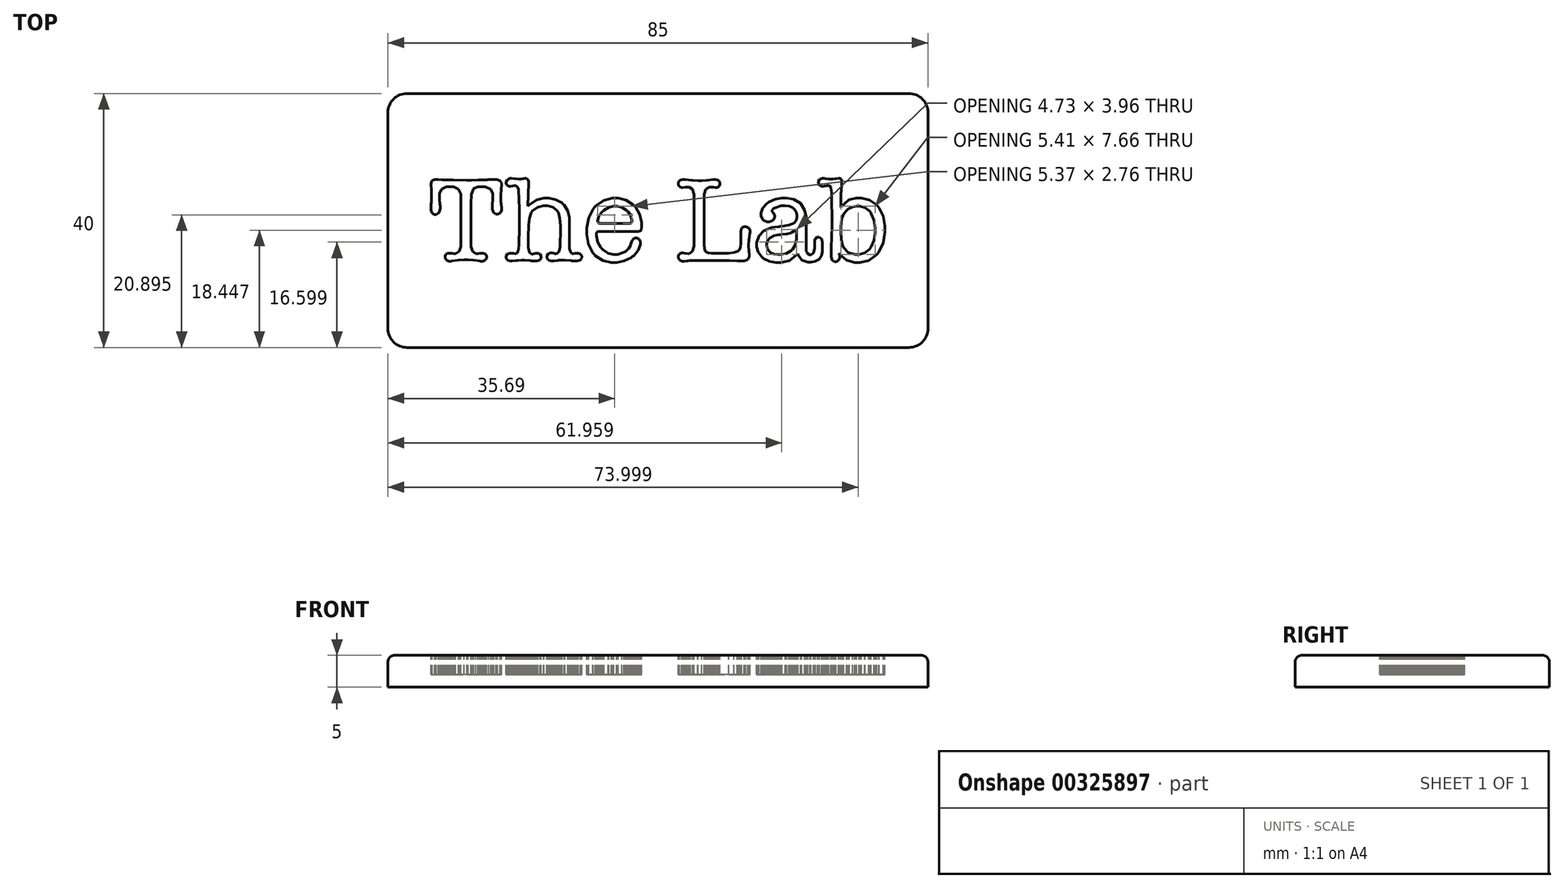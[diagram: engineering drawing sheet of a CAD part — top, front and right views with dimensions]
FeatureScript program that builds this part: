
annotation { "Feature Type Name" : "Feature", "Feature Type Description" : "" }
export const myFeature = defineFeature(function(context is Context, id is Id, definition is map)
    precondition{}
    {
        {
            var Q0;
            Q0=qCreatedBy(makeId("Top.planeOp"),FACE);
            var sketch = newSketch(context, id + "F0", { "sketchPlane" : qUnion([Q0])});
            skLineSegment(sketch, "E0", {"start": v(-29.44, -3.8) * mm, "end": v(-29.44, -4.07) * mm});
            skLineSegment(sketch, "E1", {"start": v(-29.44, -4.07) * mm, "end": v(-29.2, -4.87) * mm});
            skLineSegment(sketch, "E2", {"start": v(-29.2, -4.87) * mm, "end": v(-28.65, -5.23) * mm});
            skLineSegment(sketch, "E3", {"start": v(-28.65, -5.23) * mm, "end": v(-28.47, -5.23) * mm});
            skLineSegment(sketch, "E4", {"start": v(-28.47, -5.23) * mm, "end": v(-28.36, -5.23) * mm});
            skLineSegment(sketch, "E5", {"start": v(-28.36, -5.23) * mm, "end": v(-28.06, -5.19) * mm});
            skLineSegment(sketch, "E6", {"start": v(-28.06, -5.19) * mm, "end": v(-28.01, -5.18) * mm});
            skLineSegment(sketch, "E7", {"start": v(-28.01, -5.18) * mm, "end": v(-27.96, -5.17) * mm});
            skLineSegment(sketch, "E8", {"start": v(-27.96, -5.17) * mm, "end": v(-27.66, -5.13) * mm});
            skLineSegment(sketch, "E9", {"start": v(-27.66, -5.13) * mm, "end": v(-27.56, -5.13) * mm});
            skLineSegment(sketch, "E10", {"start": v(-27.56, -5.13) * mm, "end": v(-27.45, -5.13) * mm});
            skLineSegment(sketch, "E11", {"start": v(-27.45, -5.13) * mm, "end": v(-27.16, -5.28) * mm});
            skLineSegment(sketch, "E12", {"start": v(-27.16, -5.28) * mm, "end": v(-27.13, -5.31) * mm});
            skLineSegment(sketch, "E13", {"start": v(-27.13, -5.31) * mm, "end": v(-27.1, -5.34) * mm});
            skLineSegment(sketch, "E14", {"start": v(-27.1, -5.34) * mm, "end": v(-26.95, -5.64) * mm});
            skLineSegment(sketch, "E15", {"start": v(-26.95, -5.64) * mm, "end": v(-26.95, -5.74) * mm});
            skLineSegment(sketch, "E16", {"start": v(-26.95, -5.74) * mm, "end": v(-26.95, -5.87) * mm});
            skLineSegment(sketch, "E17", {"start": v(-26.95, -5.87) * mm, "end": v(-27.16, -6.24) * mm});
            skLineSegment(sketch, "E18", {"start": v(-27.16, -6.24) * mm, "end": v(-27.64, -6.4) * mm});
            skLineSegment(sketch, "E19", {"start": v(-27.64, -6.4) * mm, "end": v(-27.8, -6.4) * mm});
            skLineSegment(sketch, "E20", {"start": v(-27.8, -6.4) * mm, "end": v(-27.92, -6.4) * mm});
            skLineSegment(sketch, "E21", {"start": v(-27.92, -6.4) * mm, "end": v(-27.93, -6.4) * mm});
            skLineSegment(sketch, "E22", {"start": v(-27.93, -6.4) * mm, "end": v(-28.02, -6.4) * mm});
            skLineSegment(sketch, "E23", {"start": v(-28.02, -6.4) * mm, "end": v(-28.05, -6.4) * mm});
            skLineSegment(sketch, "E24", {"start": v(-28.05, -6.4) * mm, "end": v(-28.98, -6.26) * mm});
            skLineSegment(sketch, "E25", {"start": v(-28.98, -6.26) * mm, "end": v(-29.07, -6.24) * mm});
            skLineSegment(sketch, "E26", {"start": v(-29.07, -6.24) * mm, "end": v(-29.9, -6.18) * mm});
            skLineSegment(sketch, "E27", {"start": v(-29.9, -6.18) * mm, "end": v(-30.18, -6.18) * mm});
            skLineSegment(sketch, "E28", {"start": v(-30.18, -6.18) * mm, "end": v(-30.5, -6.18) * mm});
            skLineSegment(sketch, "E29", {"start": v(-30.5, -6.18) * mm, "end": v(-31.37, -6.24) * mm});
            skLineSegment(sketch, "E30", {"start": v(-31.37, -6.24) * mm, "end": v(-31.46, -6.26) * mm});
            skLineSegment(sketch, "E31", {"start": v(-31.46, -6.26) * mm, "end": v(-32.41, -6.4) * mm});
            skLineSegment(sketch, "E32", {"start": v(-32.41, -6.4) * mm, "end": v(-32.45, -6.4) * mm});
            skLineSegment(sketch, "E33", {"start": v(-32.45, -6.4) * mm, "end": v(-32.53, -6.4) * mm});
            skLineSegment(sketch, "E34", {"start": v(-32.53, -6.4) * mm, "end": v(-32.55, -6.4) * mm});
            skLineSegment(sketch, "E35", {"start": v(-32.55, -6.4) * mm, "end": v(-32.68, -6.4) * mm});
            skLineSegment(sketch, "E36", {"start": v(-32.68, -6.4) * mm, "end": v(-32.84, -6.4) * mm});
            skLineSegment(sketch, "E37", {"start": v(-32.84, -6.4) * mm, "end": v(-33.3, -6.24) * mm});
            skLineSegment(sketch, "E38", {"start": v(-33.3, -6.24) * mm, "end": v(-33.52, -5.87) * mm});
            skLineSegment(sketch, "E39", {"start": v(-33.52, -5.87) * mm, "end": v(-33.52, -5.74) * mm});
            skLineSegment(sketch, "E40", {"start": v(-33.52, -5.74) * mm, "end": v(-33.52, -5.63) * mm});
            skLineSegment(sketch, "E41", {"start": v(-33.52, -5.63) * mm, "end": v(-33.37, -5.29) * mm});
            skLineSegment(sketch, "E42", {"start": v(-33.37, -5.29) * mm, "end": v(-33.02, -5.13) * mm});
            skLineSegment(sketch, "E43", {"start": v(-33.02, -5.13) * mm, "end": v(-32.9, -5.13) * mm});
            skLineSegment(sketch, "E44", {"start": v(-32.9, -5.13) * mm, "end": v(-32.8, -5.13) * mm});
            skLineSegment(sketch, "E45", {"start": v(-32.8, -5.13) * mm, "end": v(-32.5, -5.17) * mm});
            skLineSegment(sketch, "E46", {"start": v(-32.5, -5.17) * mm, "end": v(-32.45, -5.18) * mm});
            skLineSegment(sketch, "E47", {"start": v(-32.45, -5.18) * mm, "end": v(-32.4, -5.19) * mm});
            skLineSegment(sketch, "E48", {"start": v(-32.4, -5.19) * mm, "end": v(-32.1, -5.23) * mm});
            skLineSegment(sketch, "E49", {"start": v(-32.1, -5.23) * mm, "end": v(-32, -5.23) * mm});
            skLineSegment(sketch, "E50", {"start": v(-32, -5.23) * mm, "end": v(-31.82, -5.23) * mm});
            skLineSegment(sketch, "E51", {"start": v(-31.82, -5.23) * mm, "end": v(-31.28, -4.87) * mm});
            skLineSegment(sketch, "E52", {"start": v(-31.28, -4.87) * mm, "end": v(-31.04, -4.07) * mm});
            skLineSegment(sketch, "E53", {"start": v(-31.04, -4.07) * mm, "end": v(-31.04, -3.8) * mm});
            skLineSegment(sketch, "E54", {"start": v(-31.04, -3.8) * mm, "end": v(-31.04, -2.47) * mm});
            skLineSegment(sketch, "E55", {"start": v(-31.04, -2.47) * mm, "end": v(-31.02, -0.8) * mm});
            skLineSegment(sketch, "E56", {"start": v(-31.02, -0.8) * mm, "end": v(-31.02, 0.83) * mm});
            skLineSegment(sketch, "E57", {"start": v(-31.02, 0.83) * mm, "end": v(-31.04, 3.93) * mm});
            skLineSegment(sketch, "E58", {"start": v(-31.04, 3.93) * mm, "end": v(-31.04, 4.19) * mm});
            skLineSegment(sketch, "E59", {"start": v(-31.04, 4.19) * mm, "end": v(-31.39, 4.95) * mm});
            skLineSegment(sketch, "E60", {"start": v(-31.39, 4.95) * mm, "end": v(-32.17, 5.29) * mm});
            skLineSegment(sketch, "E61", {"start": v(-32.17, 5.29) * mm, "end": v(-32.43, 5.29) * mm});
            skLineSegment(sketch, "E62", {"start": v(-32.43, 5.29) * mm, "end": v(-33.02, 5.29) * mm});
            skLineSegment(sketch, "E63", {"start": v(-33.02, 5.29) * mm, "end": v(-33.28, 5.29) * mm});
            skLineSegment(sketch, "E64", {"start": v(-33.28, 5.29) * mm, "end": v(-34.05, 4.95) * mm});
            skLineSegment(sketch, "E65", {"start": v(-34.05, 4.95) * mm, "end": v(-34.4, 4.2) * mm});
            skLineSegment(sketch, "E66", {"start": v(-34.4, 4.2) * mm, "end": v(-34.4, 3.95) * mm});
            skLineSegment(sketch, "E67", {"start": v(-34.4, 3.95) * mm, "end": v(-34.4, 3.8) * mm});
            skLineSegment(sketch, "E68", {"start": v(-34.4, 3.8) * mm, "end": v(-34.38, 3.33) * mm});
            skLineSegment(sketch, "E69", {"start": v(-34.38, 3.33) * mm, "end": v(-34.38, 3.3) * mm});
            skLineSegment(sketch, "E70", {"start": v(-34.38, 3.3) * mm, "end": v(-34.3, 2.6) * mm});
            skLineSegment(sketch, "E71", {"start": v(-34.3, 2.6) * mm, "end": v(-34.3, 2.57) * mm});
            skLineSegment(sketch, "E72", {"start": v(-34.3, 2.57) * mm, "end": v(-34.28, 2.24) * mm});
            skLineSegment(sketch, "E73", {"start": v(-34.28, 2.24) * mm, "end": v(-34.28, 2.12) * mm});
            skLineSegment(sketch, "E74", {"start": v(-34.28, 2.12) * mm, "end": v(-34.28, 1.9) * mm});
            skLineSegment(sketch, "E75", {"start": v(-34.28, 1.9) * mm, "end": v(-34.47, 1.22) * mm});
            skLineSegment(sketch, "E76", {"start": v(-34.47, 1.22) * mm, "end": v(-34.88, 0.92) * mm});
            skLineSegment(sketch, "E77", {"start": v(-34.88, 0.92) * mm, "end": v(-35.02, 0.92) * mm});
            skLineSegment(sketch, "E78", {"start": v(-35.02, 0.92) * mm, "end": v(-35.16, 0.92) * mm});
            skLineSegment(sketch, "E79", {"start": v(-35.16, 0.92) * mm, "end": v(-35.55, 1.14) * mm});
            skLineSegment(sketch, "E80", {"start": v(-35.55, 1.14) * mm, "end": v(-35.73, 1.64) * mm});
            skLineSegment(sketch, "E81", {"start": v(-35.73, 1.64) * mm, "end": v(-35.73, 1.8) * mm});
            skLineSegment(sketch, "E82", {"start": v(-35.73, 1.8) * mm, "end": v(-35.73, 2.02) * mm});
            skLineSegment(sketch, "E83", {"start": v(-35.73, 2.02) * mm, "end": v(-35.7, 2.56) * mm});
            skLineSegment(sketch, "E84", {"start": v(-35.7, 2.56) * mm, "end": v(-35.7, 2.66) * mm});
            skLineSegment(sketch, "E85", {"start": v(-35.7, 2.66) * mm, "end": v(-35.68, 2.81) * mm});
            skLineSegment(sketch, "E86", {"start": v(-35.68, 2.81) * mm, "end": v(-35.65, 3.4) * mm});
            skLineSegment(sketch, "E87", {"start": v(-35.65, 3.4) * mm, "end": v(-35.63, 3.72) * mm});
            skLineSegment(sketch, "E88", {"start": v(-35.63, 3.72) * mm, "end": v(-35.63, 3.82) * mm});
            skLineSegment(sketch, "E89", {"start": v(-35.63, 3.82) * mm, "end": v(-35.63, 4.07) * mm});
            skLineSegment(sketch, "E90", {"start": v(-35.63, 4.07) * mm, "end": v(-35.67, 4.72) * mm});
            skLineSegment(sketch, "E91", {"start": v(-35.67, 4.72) * mm, "end": v(-35.67, 4.81) * mm});
            skLineSegment(sketch, "E92", {"start": v(-35.67, 4.81) * mm, "end": v(-35.68, 4.98) * mm});
            skLineSegment(sketch, "E93", {"start": v(-35.68, 4.98) * mm, "end": v(-35.73, 5.53) * mm});
            skLineSegment(sketch, "E94", {"start": v(-35.73, 5.53) * mm, "end": v(-35.75, 5.67) * mm});
            skLineSegment(sketch, "E95", {"start": v(-35.75, 5.67) * mm, "end": v(-35.75, 5.82) * mm});
            skLineSegment(sketch, "E96", {"start": v(-35.75, 5.82) * mm, "end": v(-35.57, 6.27) * mm});
            skLineSegment(sketch, "E97", {"start": v(-35.57, 6.27) * mm, "end": v(-35.16, 6.47) * mm});
            skLineSegment(sketch, "E98", {"start": v(-35.16, 6.47) * mm, "end": v(-35.02, 6.47) * mm});
            skLineSegment(sketch, "E99", {"start": v(-35.02, 6.47) * mm, "end": v(-34.91, 6.47) * mm});
            skLineSegment(sketch, "E100", {"start": v(-34.91, 6.47) * mm, "end": v(-34.58, 6.45) * mm});
            skLineSegment(sketch, "E101", {"start": v(-34.58, 6.45) * mm, "end": v(-33.95, 6.42) * mm});
            skLineSegment(sketch, "E102", {"start": v(-33.95, 6.42) * mm, "end": v(-33.78, 6.4) * mm});
            skLineSegment(sketch, "E103", {"start": v(-33.78, 6.4) * mm, "end": v(-33.68, 6.4) * mm});
            skLineSegment(sketch, "E104", {"start": v(-33.68, 6.4) * mm, "end": v(-33.35, 6.4) * mm});
            skLineSegment(sketch, "E105", {"start": v(-33.35, 6.4) * mm, "end": v(-32.47, 6.38) * mm});
            skLineSegment(sketch, "E106", {"start": v(-32.47, 6.38) * mm, "end": v(-32.22, 6.37) * mm});
            skLineSegment(sketch, "E107", {"start": v(-32.22, 6.37) * mm, "end": v(-30.05, 6.33) * mm});
            skLineSegment(sketch, "E108", {"start": v(-30.05, 6.33) * mm, "end": v(-29.88, 6.33) * mm});
            skLineSegment(sketch, "E109", {"start": v(-29.88, 6.33) * mm, "end": v(-29.35, 6.34) * mm});
            skLineSegment(sketch, "E110", {"start": v(-29.35, 6.34) * mm, "end": v(-28.29, 6.37) * mm});
            skLineSegment(sketch, "E111", {"start": v(-28.29, 6.37) * mm, "end": v(-28.01, 6.37) * mm});
            skLineSegment(sketch, "E112", {"start": v(-28.01, 6.37) * mm, "end": v(-27.7, 6.37) * mm});
            skLineSegment(sketch, "E113", {"start": v(-27.7, 6.37) * mm, "end": v(-26.92, 6.42) * mm});
            skLineSegment(sketch, "E114", {"start": v(-26.92, 6.42) * mm, "end": v(-26.77, 6.43) * mm});
            skLineSegment(sketch, "E115", {"start": v(-26.77, 6.43) * mm, "end": v(-26.65, 6.44) * mm});
            skLineSegment(sketch, "E116", {"start": v(-26.65, 6.44) * mm, "end": v(-25.83, 6.49) * mm});
            skLineSegment(sketch, "E117", {"start": v(-25.83, 6.49) * mm, "end": v(-25.55, 6.49) * mm});
            skLineSegment(sketch, "E118", {"start": v(-25.55, 6.49) * mm, "end": v(-25.38, 6.49) * mm});
            skLineSegment(sketch, "E119", {"start": v(-25.38, 6.49) * mm, "end": v(-24.84, 6.3) * mm});
            skLineSegment(sketch, "E120", {"start": v(-24.84, 6.3) * mm, "end": v(-24.6, 5.85) * mm});
            skLineSegment(sketch, "E121", {"start": v(-24.6, 5.85) * mm, "end": v(-24.6, 5.7) * mm});
            skLineSegment(sketch, "E122", {"start": v(-24.6, 5.7) * mm, "end": v(-24.6, 5.67) * mm});
            skLineSegment(sketch, "E123", {"start": v(-24.6, 5.67) * mm, "end": v(-24.6, 5.5) * mm});
            skLineSegment(sketch, "E124", {"start": v(-24.6, 5.5) * mm, "end": v(-24.64, 5.05) * mm});
            skLineSegment(sketch, "E125", {"start": v(-24.64, 5.05) * mm, "end": v(-24.65, 4.96) * mm});
            skLineSegment(sketch, "E126", {"start": v(-24.65, 4.96) * mm, "end": v(-24.66, 4.88) * mm});
            skLineSegment(sketch, "E127", {"start": v(-24.66, 4.88) * mm, "end": v(-24.75, 3.96) * mm});
            skLineSegment(sketch, "E128", {"start": v(-24.75, 3.96) * mm, "end": v(-24.76, 3.86) * mm});
            skLineSegment(sketch, "E129", {"start": v(-24.76, 3.86) * mm, "end": v(-24.76, 3.65) * mm});
            skLineSegment(sketch, "E130", {"start": v(-24.76, 3.65) * mm, "end": v(-24.76, 3.43) * mm});
            skLineSegment(sketch, "E131", {"start": v(-24.76, 3.43) * mm, "end": v(-24.7, 2.85) * mm});
            skLineSegment(sketch, "E132", {"start": v(-24.7, 2.85) * mm, "end": v(-24.7, 2.75) * mm});
            skLineSegment(sketch, "E133", {"start": v(-24.7, 2.75) * mm, "end": v(-24.69, 2.62) * mm});
            skLineSegment(sketch, "E134", {"start": v(-24.69, 2.62) * mm, "end": v(-24.62, 1.98) * mm});
            skLineSegment(sketch, "E135", {"start": v(-24.62, 1.98) * mm, "end": v(-24.62, 1.76) * mm});
            skLineSegment(sketch, "E136", {"start": v(-24.62, 1.76) * mm, "end": v(-24.62, 1.62) * mm});
            skLineSegment(sketch, "E137", {"start": v(-24.62, 1.62) * mm, "end": v(-24.8, 1.18) * mm});
            skLineSegment(sketch, "E138", {"start": v(-24.8, 1.18) * mm, "end": v(-25.23, 0.98) * mm});
            skLineSegment(sketch, "E139", {"start": v(-25.23, 0.98) * mm, "end": v(-25.36, 0.98) * mm});
            skLineSegment(sketch, "E140", {"start": v(-25.36, 0.98) * mm, "end": v(-25.5, 0.98) * mm});
            skLineSegment(sketch, "E141", {"start": v(-25.5, 0.98) * mm, "end": v(-25.9, 1.22) * mm});
            skLineSegment(sketch, "E142", {"start": v(-25.9, 1.22) * mm, "end": v(-26.09, 1.75) * mm});
            skLineSegment(sketch, "E143", {"start": v(-26.09, 1.75) * mm, "end": v(-26.09, 1.93) * mm});
            skLineSegment(sketch, "E144", {"start": v(-26.09, 1.93) * mm, "end": v(-26.09, 2.19) * mm});
            skLineSegment(sketch, "E145", {"start": v(-26.09, 2.19) * mm, "end": v(-26.04, 2.84) * mm});
            skLineSegment(sketch, "E146", {"start": v(-26.04, 2.84) * mm, "end": v(-26.03, 2.95) * mm});
            skLineSegment(sketch, "E147", {"start": v(-26.03, 2.95) * mm, "end": v(-26.02, 3.07) * mm});
            skLineSegment(sketch, "E148", {"start": v(-26.02, 3.07) * mm, "end": v(-25.97, 3.75) * mm});
            skLineSegment(sketch, "E149", {"start": v(-25.97, 3.75) * mm, "end": v(-25.97, 3.97) * mm});
            skLineSegment(sketch, "E150", {"start": v(-25.97, 3.97) * mm, "end": v(-25.97, 4.22) * mm});
            skLineSegment(sketch, "E151", {"start": v(-25.97, 4.22) * mm, "end": v(-26.35, 4.96) * mm});
            skLineSegment(sketch, "E152", {"start": v(-26.35, 4.96) * mm, "end": v(-27.2, 5.29) * mm});
            skLineSegment(sketch, "E153", {"start": v(-27.2, 5.29) * mm, "end": v(-27.48, 5.29) * mm});
            skLineSegment(sketch, "E154", {"start": v(-27.48, 5.29) * mm, "end": v(-28.01, 5.29) * mm});
            skLineSegment(sketch, "E155", {"start": v(-28.01, 5.29) * mm, "end": v(-28.27, 5.29) * mm});
            skLineSegment(sketch, "E156", {"start": v(-28.27, 5.29) * mm, "end": v(-28.97, 5.04) * mm});
            skLineSegment(sketch, "E157", {"start": v(-28.97, 5.04) * mm, "end": v(-29.02, 5) * mm});
            skLineSegment(sketch, "E158", {"start": v(-29.02, 5) * mm, "end": v(-29.07, 4.94) * mm});
            skLineSegment(sketch, "E159", {"start": v(-29.07, 4.94) * mm, "end": v(-29.36, 4.12) * mm});
            skLineSegment(sketch, "E160", {"start": v(-29.36, 4.12) * mm, "end": v(-29.37, 4) * mm});
            skLineSegment(sketch, "E161", {"start": v(-29.37, 4) * mm, "end": v(-29.42, 2.68) * mm});
            skLineSegment(sketch, "E162", {"start": v(-29.42, 2.68) * mm, "end": v(-29.44, -3.8) * mm});
            skLineSegment(sketch, "E163", {"start": v(-20.37, 5.95) * mm, "end": v(-20.45, 2.26) * mm});
            skLineSegment(sketch, "E164", {"start": v(-20.45, 2.26) * mm, "end": v(-20.32, 2.38) * mm});
            skLineSegment(sketch, "E165", {"start": v(-20.32, 2.38) * mm, "end": v(-19.16, 3.21) * mm});
            skLineSegment(sketch, "E166", {"start": v(-19.16, 3.21) * mm, "end": v(-19.06, 3.26) * mm});
            skLineSegment(sketch, "E167", {"start": v(-19.06, 3.26) * mm, "end": v(-18.95, 3.3) * mm});
            skLineSegment(sketch, "E168", {"start": v(-18.95, 3.3) * mm, "end": v(-17.92, 3.53) * mm});
            skLineSegment(sketch, "E169", {"start": v(-17.92, 3.53) * mm, "end": v(-17.57, 3.53) * mm});
            skLineSegment(sketch, "E170", {"start": v(-17.57, 3.53) * mm, "end": v(-17.2, 3.53) * mm});
            skLineSegment(sketch, "E171", {"start": v(-17.2, 3.53) * mm, "end": v(-16.1, 3.3) * mm});
            skLineSegment(sketch, "E172", {"start": v(-16.1, 3.3) * mm, "end": v(-15.1, 2.76) * mm});
            skLineSegment(sketch, "E173", {"start": v(-15.1, 2.76) * mm, "end": v(-14.94, 2.6) * mm});
            skLineSegment(sketch, "E174", {"start": v(-14.94, 2.6) * mm, "end": v(-14.78, 2.45) * mm});
            skLineSegment(sketch, "E175", {"start": v(-14.78, 2.45) * mm, "end": v(-14.2, 1.52) * mm});
            skLineSegment(sketch, "E176", {"start": v(-14.2, 1.52) * mm, "end": v(-13.95, 0.49) * mm});
            skLineSegment(sketch, "E177", {"start": v(-13.95, 0.49) * mm, "end": v(-13.95, 0.14) * mm});
            skLineSegment(sketch, "E178", {"start": v(-13.95, 0.14) * mm, "end": v(-13.95, -3.04) * mm});
            skLineSegment(sketch, "E179", {"start": v(-13.95, -3.04) * mm, "end": v(-13.95, -3.26) * mm});
            skLineSegment(sketch, "E180", {"start": v(-13.95, -3.26) * mm, "end": v(-13.95, -3.91) * mm});
            skLineSegment(sketch, "E181", {"start": v(-13.95, -3.91) * mm, "end": v(-13.94, -4.26) * mm});
            skLineSegment(sketch, "E182", {"start": v(-13.94, -4.26) * mm, "end": v(-13.94, -4.28) * mm});
            skLineSegment(sketch, "E183", {"start": v(-13.94, -4.28) * mm, "end": v(-13.92, -4.44) * mm});
            skLineSegment(sketch, "E184", {"start": v(-13.92, -4.44) * mm, "end": v(-13.77, -5) * mm});
            skLineSegment(sketch, "E185", {"start": v(-13.77, -5) * mm, "end": v(-13.52, -5.23) * mm});
            skLineSegment(sketch, "E186", {"start": v(-13.52, -5.23) * mm, "end": v(-13.44, -5.23) * mm});
            skLineSegment(sketch, "E187", {"start": v(-13.44, -5.23) * mm, "end": v(-13.33, -5.23) * mm});
            skLineSegment(sketch, "E188", {"start": v(-13.33, -5.23) * mm, "end": v(-13.05, -5.17) * mm});
            skLineSegment(sketch, "E189", {"start": v(-13.05, -5.17) * mm, "end": v(-13, -5.15) * mm});
            skLineSegment(sketch, "E190", {"start": v(-13, -5.15) * mm, "end": v(-12.98, -5.15) * mm});
            skLineSegment(sketch, "E191", {"start": v(-12.98, -5.15) * mm, "end": v(-12.77, -5.13) * mm});
            skLineSegment(sketch, "E192", {"start": v(-12.77, -5.13) * mm, "end": v(-12.7, -5.13) * mm});
            skLineSegment(sketch, "E193", {"start": v(-12.7, -5.13) * mm, "end": v(-12.57, -5.13) * mm});
            skLineSegment(sketch, "E194", {"start": v(-12.57, -5.13) * mm, "end": v(-12.17, -5.3) * mm});
            skLineSegment(sketch, "E195", {"start": v(-12.17, -5.3) * mm, "end": v(-12, -5.64) * mm});
            skLineSegment(sketch, "E196", {"start": v(-12, -5.64) * mm, "end": v(-12, -5.76) * mm});
            skLineSegment(sketch, "E197", {"start": v(-12, -5.76) * mm, "end": v(-12, -5.88) * mm});
            skLineSegment(sketch, "E198", {"start": v(-12, -5.88) * mm, "end": v(-12.22, -6.23) * mm});
            skLineSegment(sketch, "E199", {"start": v(-12.22, -6.23) * mm, "end": v(-12.74, -6.4) * mm});
            skLineSegment(sketch, "E200", {"start": v(-12.74, -6.4) * mm, "end": v(-12.9, -6.4) * mm});
            skLineSegment(sketch, "E201", {"start": v(-12.9, -6.4) * mm, "end": v(-13.09, -6.4) * mm});
            skLineSegment(sketch, "E202", {"start": v(-13.09, -6.4) * mm, "end": v(-13.55, -6.34) * mm});
            skLineSegment(sketch, "E203", {"start": v(-13.55, -6.34) * mm, "end": v(-13.63, -6.33) * mm});
            skLineSegment(sketch, "E204", {"start": v(-13.63, -6.33) * mm, "end": v(-13.76, -6.32) * mm});
            skLineSegment(sketch, "E205", {"start": v(-13.76, -6.32) * mm, "end": v(-14.64, -6.24) * mm});
            skLineSegment(sketch, "E206", {"start": v(-14.64, -6.24) * mm, "end": v(-14.92, -6.24) * mm});
            skLineSegment(sketch, "E207", {"start": v(-14.92, -6.24) * mm, "end": v(-15.12, -6.24) * mm});
            skLineSegment(sketch, "E208", {"start": v(-15.12, -6.24) * mm, "end": v(-15.64, -6.27) * mm});
            skLineSegment(sketch, "E209", {"start": v(-15.64, -6.27) * mm, "end": v(-15.69, -6.28) * mm});
            skLineSegment(sketch, "E210", {"start": v(-15.69, -6.28) * mm, "end": v(-15.82, -6.3) * mm});
            skLineSegment(sketch, "E211", {"start": v(-15.82, -6.3) * mm, "end": v(-16.34, -6.36) * mm});
            skLineSegment(sketch, "E212", {"start": v(-16.34, -6.36) * mm, "end": v(-16.6, -6.4) * mm});
            skLineSegment(sketch, "E213", {"start": v(-16.6, -6.4) * mm, "end": v(-16.68, -6.4) * mm});
            skLineSegment(sketch, "E214", {"start": v(-16.68, -6.4) * mm, "end": v(-16.82, -6.4) * mm});
            skLineSegment(sketch, "E215", {"start": v(-16.82, -6.4) * mm, "end": v(-17.21, -6.22) * mm});
            skLineSegment(sketch, "E216", {"start": v(-17.21, -6.22) * mm, "end": v(-17.25, -6.2) * mm});
            skLineSegment(sketch, "E217", {"start": v(-17.25, -6.2) * mm, "end": v(-17.29, -6.16) * mm});
            skLineSegment(sketch, "E218", {"start": v(-17.29, -6.16) * mm, "end": v(-17.48, -5.8) * mm});
            skLineSegment(sketch, "E219", {"start": v(-17.48, -5.8) * mm, "end": v(-17.48, -5.69) * mm});
            skLineSegment(sketch, "E220", {"start": v(-17.48, -5.69) * mm, "end": v(-17.48, -5.58) * mm});
            skLineSegment(sketch, "E221", {"start": v(-17.48, -5.58) * mm, "end": v(-17.31, -5.3) * mm});
            skLineSegment(sketch, "E222", {"start": v(-17.31, -5.3) * mm, "end": v(-17.28, -5.27) * mm});
            skLineSegment(sketch, "E223", {"start": v(-17.28, -5.27) * mm, "end": v(-17.25, -5.24) * mm});
            skLineSegment(sketch, "E224", {"start": v(-17.25, -5.24) * mm, "end": v(-16.92, -5.1) * mm});
            skLineSegment(sketch, "E225", {"start": v(-16.92, -5.1) * mm, "end": v(-16.81, -5.1) * mm});
            skLineSegment(sketch, "E226", {"start": v(-16.81, -5.1) * mm, "end": v(-16.69, -5.1) * mm});
            skLineSegment(sketch, "E227", {"start": v(-16.69, -5.1) * mm, "end": v(-16.36, -5.18) * mm});
            skLineSegment(sketch, "E228", {"start": v(-16.36, -5.18) * mm, "end": v(-16.32, -5.2) * mm});
            skLineSegment(sketch, "E229", {"start": v(-16.32, -5.2) * mm, "end": v(-16.29, -5.2) * mm});
            skLineSegment(sketch, "E230", {"start": v(-16.29, -5.2) * mm, "end": v(-16.07, -5.25) * mm});
            skLineSegment(sketch, "E231", {"start": v(-16.07, -5.25) * mm, "end": v(-16, -5.25) * mm});
            skLineSegment(sketch, "E232", {"start": v(-16, -5.25) * mm, "end": v(-15.89, -5.25) * mm});
            skLineSegment(sketch, "E233", {"start": v(-15.89, -5.25) * mm, "end": v(-15.56, -4.94) * mm});
            skLineSegment(sketch, "E234", {"start": v(-15.56, -4.94) * mm, "end": v(-15.4, -4.22) * mm});
            skLineSegment(sketch, "E235", {"start": v(-15.4, -4.22) * mm, "end": v(-15.4, -4.01) * mm});
            skLineSegment(sketch, "E236", {"start": v(-15.4, -4.01) * mm, "end": v(-15.4, -3.79) * mm});
            skLineSegment(sketch, "E237", {"start": v(-15.4, -3.79) * mm, "end": v(-15.39, -3.23) * mm});
            skLineSegment(sketch, "E238", {"start": v(-15.39, -3.23) * mm, "end": v(-15.38, -3.12) * mm});
            skLineSegment(sketch, "E239", {"start": v(-15.38, -3.12) * mm, "end": v(-15.36, -2.3) * mm});
            skLineSegment(sketch, "E240", {"start": v(-15.36, -2.3) * mm, "end": v(-15.36, -1.27) * mm});
            skLineSegment(sketch, "E241", {"start": v(-15.36, -1.27) * mm, "end": v(-15.36, -0.86) * mm});
            skLineSegment(sketch, "E242", {"start": v(-15.36, -0.86) * mm, "end": v(-15.46, 0.36) * mm});
            skLineSegment(sketch, "E243", {"start": v(-15.46, 0.36) * mm, "end": v(-15.68, 1.23) * mm});
            skLineSegment(sketch, "E244", {"start": v(-15.68, 1.23) * mm, "end": v(-15.74, 1.34) * mm});
            skLineSegment(sketch, "E245", {"start": v(-15.74, 1.34) * mm, "end": v(-15.84, 1.5) * mm});
            skLineSegment(sketch, "E246", {"start": v(-15.84, 1.5) * mm, "end": v(-16.5, 2.09) * mm});
            skLineSegment(sketch, "E247", {"start": v(-16.5, 2.09) * mm, "end": v(-17.4, 2.33) * mm});
            skLineSegment(sketch, "E248", {"start": v(-17.4, 2.33) * mm, "end": v(-17.69, 2.33) * mm});
            skLineSegment(sketch, "E249", {"start": v(-17.69, 2.33) * mm, "end": v(-18.01, 2.33) * mm});
            skLineSegment(sketch, "E250", {"start": v(-18.01, 2.33) * mm, "end": v(-18.99, 2.08) * mm});
            skLineSegment(sketch, "E251", {"start": v(-18.99, 2.08) * mm, "end": v(-19.76, 1.48) * mm});
            skLineSegment(sketch, "E252", {"start": v(-19.76, 1.48) * mm, "end": v(-19.88, 1.3) * mm});
            skLineSegment(sketch, "E253", {"start": v(-19.88, 1.3) * mm, "end": v(-19.96, 1.19) * mm});
            skLineSegment(sketch, "E254", {"start": v(-19.96, 1.19) * mm, "end": v(-20.24, 0.39) * mm});
            skLineSegment(sketch, "E255", {"start": v(-20.24, 0.39) * mm, "end": v(-20.37, -0.7) * mm});
            skLineSegment(sketch, "E256", {"start": v(-20.37, -0.7) * mm, "end": v(-20.37, -0.96) * mm});
            skLineSegment(sketch, "E257", {"start": v(-20.37, -0.96) * mm, "end": v(-20.4, -2.33) * mm});
            skLineSegment(sketch, "E258", {"start": v(-20.4, -2.33) * mm, "end": v(-20.4, -2.43) * mm});
            skLineSegment(sketch, "E259", {"start": v(-20.4, -2.43) * mm, "end": v(-20.4, -2.67) * mm});
            skLineSegment(sketch, "E260", {"start": v(-20.4, -2.67) * mm, "end": v(-20.41, -2.72) * mm});
            skLineSegment(sketch, "E261", {"start": v(-20.41, -2.72) * mm, "end": v(-20.41, -3.08) * mm});
            skLineSegment(sketch, "E262", {"start": v(-20.41, -3.08) * mm, "end": v(-20.41, -3.3) * mm});
            skLineSegment(sketch, "E263", {"start": v(-20.41, -3.3) * mm, "end": v(-20.4, -3.93) * mm});
            skLineSegment(sketch, "E264", {"start": v(-20.4, -3.93) * mm, "end": v(-20.4, -4.3) * mm});
            skLineSegment(sketch, "E265", {"start": v(-20.4, -4.3) * mm, "end": v(-20.4, -4.33) * mm});
            skLineSegment(sketch, "E266", {"start": v(-20.4, -4.33) * mm, "end": v(-20.38, -4.49) * mm});
            skLineSegment(sketch, "E267", {"start": v(-20.38, -4.49) * mm, "end": v(-20.2, -5.03) * mm});
            skLineSegment(sketch, "E268", {"start": v(-20.2, -5.03) * mm, "end": v(-19.93, -5.27) * mm});
            skLineSegment(sketch, "E269", {"start": v(-19.93, -5.27) * mm, "end": v(-19.84, -5.27) * mm});
            skLineSegment(sketch, "E270", {"start": v(-19.84, -5.27) * mm, "end": v(-19.73, -5.27) * mm});
            skLineSegment(sketch, "E271", {"start": v(-19.73, -5.27) * mm, "end": v(-19.46, -5.21) * mm});
            skLineSegment(sketch, "E272", {"start": v(-19.46, -5.21) * mm, "end": v(-19.41, -5.2) * mm});
            skLineSegment(sketch, "E273", {"start": v(-19.41, -5.2) * mm, "end": v(-19.37, -5.19) * mm});
            skLineSegment(sketch, "E274", {"start": v(-19.37, -5.19) * mm, "end": v(-19.1, -5.13) * mm});
            skLineSegment(sketch, "E275", {"start": v(-19.1, -5.13) * mm, "end": v(-19, -5.13) * mm});
            skLineSegment(sketch, "E276", {"start": v(-19, -5.13) * mm, "end": v(-18.89, -5.13) * mm});
            skLineSegment(sketch, "E277", {"start": v(-18.89, -5.13) * mm, "end": v(-18.54, -5.28) * mm});
            skLineSegment(sketch, "E278", {"start": v(-18.54, -5.28) * mm, "end": v(-18.4, -5.61) * mm});
            skLineSegment(sketch, "E279", {"start": v(-18.4, -5.61) * mm, "end": v(-18.4, -5.73) * mm});
            skLineSegment(sketch, "E280", {"start": v(-18.4, -5.73) * mm, "end": v(-18.4, -5.85) * mm});
            skLineSegment(sketch, "E281", {"start": v(-18.4, -5.85) * mm, "end": v(-18.6, -6.22) * mm});
            skLineSegment(sketch, "E282", {"start": v(-18.6, -6.22) * mm, "end": v(-19.07, -6.4) * mm});
            skLineSegment(sketch, "E283", {"start": v(-19.07, -6.4) * mm, "end": v(-19.23, -6.4) * mm});
            skLineSegment(sketch, "E284", {"start": v(-19.23, -6.4) * mm, "end": v(-19.43, -6.4) * mm});
            skLineSegment(sketch, "E285", {"start": v(-19.43, -6.4) * mm, "end": v(-19.94, -6.34) * mm});
            skLineSegment(sketch, "E286", {"start": v(-19.94, -6.34) * mm, "end": v(-20.03, -6.33) * mm});
            skLineSegment(sketch, "E287", {"start": v(-20.03, -6.33) * mm, "end": v(-20.15, -6.32) * mm});
            skLineSegment(sketch, "E288", {"start": v(-20.15, -6.32) * mm, "end": v(-21, -6.26) * mm});
            skLineSegment(sketch, "E289", {"start": v(-21, -6.26) * mm, "end": v(-21.27, -6.26) * mm});
            skLineSegment(sketch, "E290", {"start": v(-21.27, -6.26) * mm, "end": v(-21.5, -6.26) * mm});
            skLineSegment(sketch, "E291", {"start": v(-21.5, -6.26) * mm, "end": v(-22.07, -6.3) * mm});
            skLineSegment(sketch, "E292", {"start": v(-22.07, -6.3) * mm, "end": v(-22.17, -6.31) * mm});
            skLineSegment(sketch, "E293", {"start": v(-22.17, -6.31) * mm, "end": v(-22.3, -6.33) * mm});
            skLineSegment(sketch, "E294", {"start": v(-22.3, -6.33) * mm, "end": v(-22.93, -6.4) * mm});
            skLineSegment(sketch, "E295", {"start": v(-22.93, -6.4) * mm, "end": v(-23.14, -6.4) * mm});
            skLineSegment(sketch, "E296", {"start": v(-23.14, -6.4) * mm, "end": v(-23.28, -6.4) * mm});
            skLineSegment(sketch, "E297", {"start": v(-23.28, -6.4) * mm, "end": v(-23.72, -6.22) * mm});
            skLineSegment(sketch, "E298", {"start": v(-23.72, -6.22) * mm, "end": v(-23.92, -5.83) * mm});
            skLineSegment(sketch, "E299", {"start": v(-23.92, -5.83) * mm, "end": v(-23.92, -5.7) * mm});
            skLineSegment(sketch, "E300", {"start": v(-23.92, -5.7) * mm, "end": v(-23.92, -5.6) * mm});
            skLineSegment(sketch, "E301", {"start": v(-23.92, -5.6) * mm, "end": v(-23.74, -5.28) * mm});
            skLineSegment(sketch, "E302", {"start": v(-23.74, -5.28) * mm, "end": v(-23.33, -5.13) * mm});
            skLineSegment(sketch, "E303", {"start": v(-23.33, -5.13) * mm, "end": v(-23.2, -5.13) * mm});
            skLineSegment(sketch, "E304", {"start": v(-23.2, -5.13) * mm, "end": v(-23.1, -5.13) * mm});
            skLineSegment(sketch, "E305", {"start": v(-23.1, -5.13) * mm, "end": v(-22.85, -5.17) * mm});
            skLineSegment(sketch, "E306", {"start": v(-22.85, -5.17) * mm, "end": v(-22.83, -5.17) * mm});
            skLineSegment(sketch, "E307", {"start": v(-22.83, -5.17) * mm, "end": v(-22.78, -5.18) * mm});
            skLineSegment(sketch, "E308", {"start": v(-22.78, -5.18) * mm, "end": v(-22.48, -5.23) * mm});
            skLineSegment(sketch, "E309", {"start": v(-22.48, -5.23) * mm, "end": v(-22.37, -5.23) * mm});
            skLineSegment(sketch, "E310", {"start": v(-22.37, -5.23) * mm, "end": v(-22.31, -5.23) * mm});
            skLineSegment(sketch, "E311", {"start": v(-22.31, -5.23) * mm, "end": v(-22.12, -5.08) * mm});
            skLineSegment(sketch, "E312", {"start": v(-22.12, -5.08) * mm, "end": v(-21.98, -4.75) * mm});
            skLineSegment(sketch, "E313", {"start": v(-21.98, -4.75) * mm, "end": v(-21.96, -4.65) * mm});
            skLineSegment(sketch, "E314", {"start": v(-21.96, -4.65) * mm, "end": v(-21.95, -4.55) * mm});
            skLineSegment(sketch, "E315", {"start": v(-21.95, -4.55) * mm, "end": v(-21.88, -3.76) * mm});
            skLineSegment(sketch, "E316", {"start": v(-21.88, -3.76) * mm, "end": v(-21.85, -2.57) * mm});
            skLineSegment(sketch, "E317", {"start": v(-21.85, -2.57) * mm, "end": v(-21.84, -2.28) * mm});
            skLineSegment(sketch, "E318", {"start": v(-21.84, -2.28) * mm, "end": v(-21.82, 1.13) * mm});
            skLineSegment(sketch, "E319", {"start": v(-21.82, 1.13) * mm, "end": v(-21.82, 1.72) * mm});
            skLineSegment(sketch, "E320", {"start": v(-21.82, 1.72) * mm, "end": v(-21.85, 3.47) * mm});
            skLineSegment(sketch, "E321", {"start": v(-21.85, 3.47) * mm, "end": v(-21.92, 4.62) * mm});
            skLineSegment(sketch, "E322", {"start": v(-21.92, 4.62) * mm, "end": v(-21.94, 4.74) * mm});
            skLineSegment(sketch, "E323", {"start": v(-21.94, 4.74) * mm, "end": v(-21.96, 4.87) * mm});
            skLineSegment(sketch, "E324", {"start": v(-21.96, 4.87) * mm, "end": v(-22.13, 5.3) * mm});
            skLineSegment(sketch, "E325", {"start": v(-22.13, 5.3) * mm, "end": v(-22.38, 5.5) * mm});
            skLineSegment(sketch, "E326", {"start": v(-22.38, 5.5) * mm, "end": v(-22.47, 5.5) * mm});
            skLineSegment(sketch, "E327", {"start": v(-22.47, 5.5) * mm, "end": v(-22.57, 5.5) * mm});
            skLineSegment(sketch, "E328", {"start": v(-22.57, 5.5) * mm, "end": v(-22.83, 5.45) * mm});
            skLineSegment(sketch, "E329", {"start": v(-22.83, 5.45) * mm, "end": v(-22.87, 5.44) * mm});
            skLineSegment(sketch, "E330", {"start": v(-22.87, 5.44) * mm, "end": v(-22.91, 5.43) * mm});
            skLineSegment(sketch, "E331", {"start": v(-22.91, 5.43) * mm, "end": v(-23.2, 5.38) * mm});
            skLineSegment(sketch, "E332", {"start": v(-23.2, 5.38) * mm, "end": v(-23.29, 5.38) * mm});
            skLineSegment(sketch, "E333", {"start": v(-23.29, 5.38) * mm, "end": v(-23.41, 5.38) * mm});
            skLineSegment(sketch, "E334", {"start": v(-23.41, 5.38) * mm, "end": v(-23.77, 5.53) * mm});
            skLineSegment(sketch, "E335", {"start": v(-23.77, 5.53) * mm, "end": v(-23.94, 5.88) * mm});
            skLineSegment(sketch, "E336", {"start": v(-23.94, 5.88) * mm, "end": v(-23.94, 6) * mm});
            skLineSegment(sketch, "E337", {"start": v(-23.94, 6) * mm, "end": v(-23.94, 6.1) * mm});
            skLineSegment(sketch, "E338", {"start": v(-23.94, 6.1) * mm, "end": v(-23.75, 6.42) * mm});
            skLineSegment(sketch, "E339", {"start": v(-23.75, 6.42) * mm, "end": v(-23.7, 6.45) * mm});
            skLineSegment(sketch, "E340", {"start": v(-23.7, 6.45) * mm, "end": v(-23.67, 6.48) * mm});
            skLineSegment(sketch, "E341", {"start": v(-23.67, 6.48) * mm, "end": v(-23.28, 6.64) * mm});
            skLineSegment(sketch, "E342", {"start": v(-23.28, 6.64) * mm, "end": v(-23.15, 6.64) * mm});
            skLineSegment(sketch, "E343", {"start": v(-23.15, 6.64) * mm, "end": v(-23, 6.64) * mm});
            skLineSegment(sketch, "E344", {"start": v(-23, 6.64) * mm, "end": v(-22.6, 6.6) * mm});
            skLineSegment(sketch, "E345", {"start": v(-22.6, 6.6) * mm, "end": v(-22.5, 6.58) * mm});
            skLineSegment(sketch, "E346", {"start": v(-22.5, 6.58) * mm, "end": v(-22.45, 6.58) * mm});
            skLineSegment(sketch, "E347", {"start": v(-22.45, 6.58) * mm, "end": v(-21.9, 6.54) * mm});
            skLineSegment(sketch, "E348", {"start": v(-21.9, 6.54) * mm, "end": v(-21.73, 6.54) * mm});
            skLineSegment(sketch, "E349", {"start": v(-21.73, 6.54) * mm, "end": v(-21.6, 6.54) * mm});
            skLineSegment(sketch, "E350", {"start": v(-21.6, 6.54) * mm, "end": v(-21.3, 6.58) * mm});
            skLineSegment(sketch, "E351", {"start": v(-21.3, 6.58) * mm, "end": v(-21.25, 6.58) * mm});
            skLineSegment(sketch, "E352", {"start": v(-21.25, 6.58) * mm, "end": v(-21.2, 6.59) * mm});
            skLineSegment(sketch, "E353", {"start": v(-21.2, 6.59) * mm, "end": v(-20.9, 6.62) * mm});
            skLineSegment(sketch, "E354", {"start": v(-20.9, 6.62) * mm, "end": v(-20.81, 6.62) * mm});
            skLineSegment(sketch, "E355", {"start": v(-20.81, 6.62) * mm, "end": v(-20.73, 6.62) * mm});
            skLineSegment(sketch, "E356", {"start": v(-20.73, 6.62) * mm, "end": v(-20.48, 6.46) * mm});
            skLineSegment(sketch, "E357", {"start": v(-20.48, 6.46) * mm, "end": v(-20.37, 6.1) * mm});
            skLineSegment(sketch, "E358", {"start": v(-20.37, 6.1) * mm, "end": v(-20.37, 6) * mm});
            skLineSegment(sketch, "E359", {"start": v(-20.37, 6) * mm, "end": v(-20.37, 5.95) * mm});
            skLineSegment(sketch, "E360", {"start": v(-2.58, -0.71) * mm, "end": v(-2.58, -0.93) * mm});
            skLineSegment(sketch, "E361", {"start": v(-2.58, -0.93) * mm, "end": v(-2.66, -1.57) * mm});
            skLineSegment(sketch, "E362", {"start": v(-2.66, -1.57) * mm, "end": v(-2.68, -1.6) * mm});
            skLineSegment(sketch, "E363", {"start": v(-2.68, -1.6) * mm, "end": v(-2.7, -1.63) * mm});
            skLineSegment(sketch, "E364", {"start": v(-2.7, -1.63) * mm, "end": v(-3.1, -1.76) * mm});
            skLineSegment(sketch, "E365", {"start": v(-3.1, -1.76) * mm, "end": v(-3.23, -1.76) * mm});
            skLineSegment(sketch, "E366", {"start": v(-3.23, -1.76) * mm, "end": v(-9.29, -1.76) * mm});
            skLineSegment(sketch, "E367", {"start": v(-9.29, -1.76) * mm, "end": v(-9.37, -1.76) * mm});
            skLineSegment(sketch, "E368", {"start": v(-9.37, -1.76) * mm, "end": v(-9.6, -1.82) * mm});
            skLineSegment(sketch, "E369", {"start": v(-9.6, -1.82) * mm, "end": v(-9.61, -1.83) * mm});
            skLineSegment(sketch, "E370", {"start": v(-9.61, -1.83) * mm, "end": v(-9.62, -1.84) * mm});
            skLineSegment(sketch, "E371", {"start": v(-9.62, -1.84) * mm, "end": v(-9.69, -2) * mm});
            skLineSegment(sketch, "E372", {"start": v(-9.69, -2) * mm, "end": v(-9.69, -2.05) * mm});
            skLineSegment(sketch, "E373", {"start": v(-9.69, -2.05) * mm, "end": v(-9.69, -2.38) * mm});
            skLineSegment(sketch, "E374", {"start": v(-9.69, -2.38) * mm, "end": v(-9.47, -3.36) * mm});
            skLineSegment(sketch, "E375", {"start": v(-9.47, -3.36) * mm, "end": v(-8.97, -4.27) * mm});
            skLineSegment(sketch, "E376", {"start": v(-8.97, -4.27) * mm, "end": v(-8.83, -4.43) * mm});
            skLineSegment(sketch, "E377", {"start": v(-8.83, -4.43) * mm, "end": v(-8.69, -4.59) * mm});
            skLineSegment(sketch, "E378", {"start": v(-8.69, -4.59) * mm, "end": v(-7.87, -5.14) * mm});
            skLineSegment(sketch, "E379", {"start": v(-7.87, -5.14) * mm, "end": v(-7, -5.38) * mm});
            skLineSegment(sketch, "E380", {"start": v(-7, -5.38) * mm, "end": v(-6.7, -5.38) * mm});
            skLineSegment(sketch, "E381", {"start": v(-6.7, -5.38) * mm, "end": v(-6.31, -5.38) * mm});
            skLineSegment(sketch, "E382", {"start": v(-6.31, -5.38) * mm, "end": v(-5.28, -5) * mm});
            skLineSegment(sketch, "E383", {"start": v(-5.28, -5) * mm, "end": v(-5.16, -4.92) * mm});
            skLineSegment(sketch, "E384", {"start": v(-5.16, -4.92) * mm, "end": v(-5.05, -4.85) * mm});
            skLineSegment(sketch, "E385", {"start": v(-5.05, -4.85) * mm, "end": v(-4.59, -4.4) * mm});
            skLineSegment(sketch, "E386", {"start": v(-4.59, -4.4) * mm, "end": v(-4.3, -3.88) * mm});
            skLineSegment(sketch, "E387", {"start": v(-4.3, -3.88) * mm, "end": v(-4.26, -3.76) * mm});
            skLineSegment(sketch, "E388", {"start": v(-4.26, -3.76) * mm, "end": v(-4.09, -3.21) * mm});
            skLineSegment(sketch, "E389", {"start": v(-4.09, -3.21) * mm, "end": v(-4.06, -3.13) * mm});
            skLineSegment(sketch, "E390", {"start": v(-4.06, -3.13) * mm, "end": v(-3.86, -2.87) * mm});
            skLineSegment(sketch, "E391", {"start": v(-3.86, -2.87) * mm, "end": v(-3.56, -2.75) * mm});
            skLineSegment(sketch, "E392", {"start": v(-3.56, -2.75) * mm, "end": v(-3.46, -2.75) * mm});
            skLineSegment(sketch, "E393", {"start": v(-3.46, -2.75) * mm, "end": v(-3.33, -2.75) * mm});
            skLineSegment(sketch, "E394", {"start": v(-3.33, -2.75) * mm, "end": v(-2.93, -2.93) * mm});
            skLineSegment(sketch, "E395", {"start": v(-2.93, -2.93) * mm, "end": v(-2.75, -3.34) * mm});
            skLineSegment(sketch, "E396", {"start": v(-2.75, -3.34) * mm, "end": v(-2.75, -3.48) * mm});
            skLineSegment(sketch, "E397", {"start": v(-2.75, -3.48) * mm, "end": v(-2.75, -3.77) * mm});
            skLineSegment(sketch, "E398", {"start": v(-2.75, -3.77) * mm, "end": v(-3.07, -4.65) * mm});
            skLineSegment(sketch, "E399", {"start": v(-3.07, -4.65) * mm, "end": v(-3.8, -5.52) * mm});
            skLineSegment(sketch, "E400", {"start": v(-3.8, -5.52) * mm, "end": v(-4, -5.68) * mm});
            skLineSegment(sketch, "E401", {"start": v(-4, -5.68) * mm, "end": v(-4.22, -5.84) * mm});
            skLineSegment(sketch, "E402", {"start": v(-4.22, -5.84) * mm, "end": v(-5.35, -6.4) * mm});
            skLineSegment(sketch, "E403", {"start": v(-5.35, -6.4) * mm, "end": v(-6.49, -6.64) * mm});
            skLineSegment(sketch, "E404", {"start": v(-6.49, -6.64) * mm, "end": v(-6.87, -6.64) * mm});
            skLineSegment(sketch, "E405", {"start": v(-6.87, -6.64) * mm, "end": v(-7.32, -6.64) * mm});
            skLineSegment(sketch, "E406", {"start": v(-7.32, -6.64) * mm, "end": v(-8.66, -6.3) * mm});
            skLineSegment(sketch, "E407", {"start": v(-8.66, -6.3) * mm, "end": v(-9.85, -5.52) * mm});
            skLineSegment(sketch, "E408", {"start": v(-9.85, -5.52) * mm, "end": v(-10.05, -5.3) * mm});
            skLineSegment(sketch, "E409", {"start": v(-10.05, -5.3) * mm, "end": v(-10.25, -5.07) * mm});
            skLineSegment(sketch, "E410", {"start": v(-10.25, -5.07) * mm, "end": v(-10.94, -3.72) * mm});
            skLineSegment(sketch, "E411", {"start": v(-10.94, -3.72) * mm, "end": v(-11.23, -2.2) * mm});
            skLineSegment(sketch, "E412", {"start": v(-11.23, -2.2) * mm, "end": v(-11.23, -1.69) * mm});
            skLineSegment(sketch, "E413", {"start": v(-11.23, -1.69) * mm, "end": v(-11.23, -1.16) * mm});
            skLineSegment(sketch, "E414", {"start": v(-11.23, -1.16) * mm, "end": v(-10.92, 0.42) * mm});
            skLineSegment(sketch, "E415", {"start": v(-10.92, 0.42) * mm, "end": v(-10.18, 1.84) * mm});
            skLineSegment(sketch, "E416", {"start": v(-10.18, 1.84) * mm, "end": v(-9.97, 2.09) * mm});
            skLineSegment(sketch, "E417", {"start": v(-9.97, 2.09) * mm, "end": v(-9.76, 2.33) * mm});
            skLineSegment(sketch, "E418", {"start": v(-9.76, 2.33) * mm, "end": v(-8.53, 3.17) * mm});
            skLineSegment(sketch, "E419", {"start": v(-8.53, 3.17) * mm, "end": v(-7.15, 3.53) * mm});
            skLineSegment(sketch, "E420", {"start": v(-7.15, 3.53) * mm, "end": v(-6.7, 3.53) * mm});
            skLineSegment(sketch, "E421", {"start": v(-6.7, 3.53) * mm, "end": v(-6.29, 3.53) * mm});
            skLineSegment(sketch, "E422", {"start": v(-6.29, 3.53) * mm, "end": v(-5.06, 3.23) * mm});
            skLineSegment(sketch, "E423", {"start": v(-5.06, 3.23) * mm, "end": v(-3.94, 2.53) * mm});
            skLineSegment(sketch, "E424", {"start": v(-3.94, 2.53) * mm, "end": v(-3.74, 2.33) * mm});
            skLineSegment(sketch, "E425", {"start": v(-3.74, 2.33) * mm, "end": v(-3.55, 2.13) * mm});
            skLineSegment(sketch, "E426", {"start": v(-3.55, 2.13) * mm, "end": v(-2.87, 0.97) * mm});
            skLineSegment(sketch, "E427", {"start": v(-2.87, 0.97) * mm, "end": v(-2.58, -0.3) * mm});
            skLineSegment(sketch, "E428", {"start": v(-2.58, -0.3) * mm, "end": v(-2.58, -0.71) * mm});
            skLineSegment(sketch, "E429", {"start": v(-9.5, -0.22) * mm, "end": v(-9.5, -0.29) * mm});
            skLineSegment(sketch, "E430", {"start": v(-9.5, -0.29) * mm, "end": v(-9.18, -0.49) * mm});
            skLineSegment(sketch, "E431", {"start": v(-9.18, -0.49) * mm, "end": v(-9.08, -0.49) * mm});
            skLineSegment(sketch, "E432", {"start": v(-9.08, -0.49) * mm, "end": v(-4.52, -0.49) * mm});
            skLineSegment(sketch, "E433", {"start": v(-4.52, -0.49) * mm, "end": v(-4.43, -0.49) * mm});
            skLineSegment(sketch, "E434", {"start": v(-4.43, -0.49) * mm, "end": v(-4.12, -0.29) * mm});
            skLineSegment(sketch, "E435", {"start": v(-4.12, -0.29) * mm, "end": v(-4.12, -0.22) * mm});
            skLineSegment(sketch, "E436", {"start": v(-4.12, -0.22) * mm, "end": v(-4.12, 0.02) * mm});
            skLineSegment(sketch, "E437", {"start": v(-4.12, 0.02) * mm, "end": v(-4.32, 0.72) * mm});
            skLineSegment(sketch, "E438", {"start": v(-4.32, 0.72) * mm, "end": v(-4.76, 1.41) * mm});
            skLineSegment(sketch, "E439", {"start": v(-4.76, 1.41) * mm, "end": v(-4.89, 1.53) * mm});
            skLineSegment(sketch, "E440", {"start": v(-4.89, 1.53) * mm, "end": v(-5.01, 1.66) * mm});
            skLineSegment(sketch, "E441", {"start": v(-5.01, 1.66) * mm, "end": v(-5.72, 2.1) * mm});
            skLineSegment(sketch, "E442", {"start": v(-5.72, 2.1) * mm, "end": v(-6.44, 2.28) * mm});
            skLineSegment(sketch, "E443", {"start": v(-6.44, 2.28) * mm, "end": v(-6.68, 2.28) * mm});
            skLineSegment(sketch, "E444", {"start": v(-6.68, 2.28) * mm, "end": v(-6.93, 2.28) * mm});
            skLineSegment(sketch, "E445", {"start": v(-6.93, 2.28) * mm, "end": v(-7.7, 2.08) * mm});
            skLineSegment(sketch, "E446", {"start": v(-7.7, 2.08) * mm, "end": v(-8.47, 1.63) * mm});
            skLineSegment(sketch, "E447", {"start": v(-8.47, 1.63) * mm, "end": v(-8.62, 1.5) * mm});
            skLineSegment(sketch, "E448", {"start": v(-8.62, 1.5) * mm, "end": v(-8.77, 1.38) * mm});
            skLineSegment(sketch, "E449", {"start": v(-8.77, 1.38) * mm, "end": v(-9.28, 0.69) * mm});
            skLineSegment(sketch, "E450", {"start": v(-9.28, 0.69) * mm, "end": v(-9.5, 0) * mm});
            skLineSegment(sketch, "E451", {"start": v(-9.5, 0) * mm, "end": v(-9.5, -0.22) * mm});
            skLineSegment(sketch, "E452", {"start": v(7.29, -3.57) * mm, "end": v(7.29, -3.8) * mm});
            skLineSegment(sketch, "E453", {"start": v(7.29, -3.8) * mm, "end": v(7.34, -4.47) * mm});
            skLineSegment(sketch, "E454", {"start": v(7.34, -4.47) * mm, "end": v(7.48, -4.87) * mm});
            skLineSegment(sketch, "E455", {"start": v(7.48, -4.87) * mm, "end": v(7.52, -4.9) * mm});
            skLineSegment(sketch, "E456", {"start": v(7.52, -4.9) * mm, "end": v(7.54, -4.93) * mm});
            skLineSegment(sketch, "E457", {"start": v(7.54, -4.93) * mm, "end": v(7.92, -5.1) * mm});
            skLineSegment(sketch, "E458", {"start": v(7.92, -5.1) * mm, "end": v(7.96, -5.11) * mm});
            skLineSegment(sketch, "E459", {"start": v(7.96, -5.11) * mm, "end": v(8, -5.12) * mm});
            skLineSegment(sketch, "E460", {"start": v(8, -5.12) * mm, "end": v(8.41, -5.14) * mm});
            skLineSegment(sketch, "E461", {"start": v(8.41, -5.14) * mm, "end": v(9.01, -5.15) * mm});
            skLineSegment(sketch, "E462", {"start": v(9.01, -5.15) * mm, "end": v(9.21, -5.15) * mm});
            skLineSegment(sketch, "E463", {"start": v(9.21, -5.15) * mm, "end": v(10.89, -5.15) * mm});
            skLineSegment(sketch, "E464", {"start": v(10.89, -5.15) * mm, "end": v(11.16, -5.15) * mm});
            skLineSegment(sketch, "E465", {"start": v(11.16, -5.15) * mm, "end": v(11.98, -5.06) * mm});
            skLineSegment(sketch, "E466", {"start": v(11.98, -5.06) * mm, "end": v(12.57, -4.86) * mm});
            skLineSegment(sketch, "E467", {"start": v(12.57, -4.86) * mm, "end": v(12.64, -4.8) * mm});
            skLineSegment(sketch, "E468", {"start": v(12.64, -4.8) * mm, "end": v(12.71, -4.74) * mm});
            skLineSegment(sketch, "E469", {"start": v(12.71, -4.74) * mm, "end": v(12.97, -4.27) * mm});
            skLineSegment(sketch, "E470", {"start": v(12.97, -4.27) * mm, "end": v(13.08, -3.6) * mm});
            skLineSegment(sketch, "E471", {"start": v(13.08, -3.6) * mm, "end": v(13.08, -3.38) * mm});
            skLineSegment(sketch, "E472", {"start": v(13.08, -3.38) * mm, "end": v(13.08, -3.21) * mm});
            skLineSegment(sketch, "E473", {"start": v(13.08, -3.21) * mm, "end": v(13.06, -2.78) * mm});
            skLineSegment(sketch, "E474", {"start": v(13.06, -2.78) * mm, "end": v(13.06, -2.72) * mm});
            skLineSegment(sketch, "E475", {"start": v(13.06, -2.72) * mm, "end": v(13.05, -2.6) * mm});
            skLineSegment(sketch, "E476", {"start": v(13.05, -2.6) * mm, "end": v(13.02, -2.01) * mm});
            skLineSegment(sketch, "E477", {"start": v(13.02, -2.01) * mm, "end": v(13.02, -1.82) * mm});
            skLineSegment(sketch, "E478", {"start": v(13.02, -1.82) * mm, "end": v(13.02, -1.66) * mm});
            skLineSegment(sketch, "E479", {"start": v(13.02, -1.66) * mm, "end": v(13.19, -1.19) * mm});
            skLineSegment(sketch, "E480", {"start": v(13.19, -1.19) * mm, "end": v(13.56, -0.98) * mm});
            skLineSegment(sketch, "E481", {"start": v(13.56, -0.98) * mm, "end": v(13.69, -0.98) * mm});
            skLineSegment(sketch, "E482", {"start": v(13.69, -0.98) * mm, "end": v(13.84, -0.98) * mm});
            skLineSegment(sketch, "E483", {"start": v(13.84, -0.98) * mm, "end": v(14.29, -1.17) * mm});
            skLineSegment(sketch, "E484", {"start": v(14.29, -1.17) * mm, "end": v(14.49, -1.6) * mm});
            skLineSegment(sketch, "E485", {"start": v(14.49, -1.6) * mm, "end": v(14.49, -1.74) * mm});
            skLineSegment(sketch, "E486", {"start": v(14.49, -1.74) * mm, "end": v(14.49, -1.83) * mm});
            skLineSegment(sketch, "E487", {"start": v(14.49, -1.83) * mm, "end": v(14.47, -2.08) * mm});
            skLineSegment(sketch, "E488", {"start": v(14.47, -2.08) * mm, "end": v(14.47, -2.1) * mm});
            skLineSegment(sketch, "E489", {"start": v(14.47, -2.1) * mm, "end": v(14.34, -3.08) * mm});
            skLineSegment(sketch, "E490", {"start": v(14.34, -3.08) * mm, "end": v(14.33, -3.15) * mm});
            skLineSegment(sketch, "E491", {"start": v(14.33, -3.15) * mm, "end": v(14.28, -3.75) * mm});
            skLineSegment(sketch, "E492", {"start": v(14.28, -3.75) * mm, "end": v(14.28, -3.95) * mm});
            skLineSegment(sketch, "E493", {"start": v(14.28, -3.95) * mm, "end": v(14.28, -4.15) * mm});
            skLineSegment(sketch, "E494", {"start": v(14.28, -4.15) * mm, "end": v(14.32, -4.66) * mm});
            skLineSegment(sketch, "E495", {"start": v(14.32, -4.66) * mm, "end": v(14.33, -4.74) * mm});
            skLineSegment(sketch, "E496", {"start": v(14.33, -4.74) * mm, "end": v(14.33, -4.83) * mm});
            skLineSegment(sketch, "E497", {"start": v(14.33, -4.83) * mm, "end": v(14.37, -5.36) * mm});
            skLineSegment(sketch, "E498", {"start": v(14.37, -5.36) * mm, "end": v(14.37, -5.53) * mm});
            skLineSegment(sketch, "E499", {"start": v(14.37, -5.53) * mm, "end": v(14.37, -5.7) * mm});
            skLineSegment(sketch, "E500", {"start": v(14.37, -5.7) * mm, "end": v(14.13, -6.18) * mm});
            skLineSegment(sketch, "E501", {"start": v(14.13, -6.18) * mm, "end": v(13.58, -6.4) * mm});
            skLineSegment(sketch, "E502", {"start": v(13.58, -6.4) * mm, "end": v(13.4, -6.4) * mm});
            skLineSegment(sketch, "E503", {"start": v(13.4, -6.4) * mm, "end": v(13.18, -6.4) * mm});
            skLineSegment(sketch, "E504", {"start": v(13.18, -6.4) * mm, "end": v(12.64, -6.36) * mm});
            skLineSegment(sketch, "E505", {"start": v(12.64, -6.36) * mm, "end": v(12.53, -6.35) * mm});
            skLineSegment(sketch, "E506", {"start": v(12.53, -6.35) * mm, "end": v(12.45, -6.35) * mm});
            skLineSegment(sketch, "E507", {"start": v(12.45, -6.35) * mm, "end": v(11.27, -6.32) * mm});
            skLineSegment(sketch, "E508", {"start": v(11.27, -6.32) * mm, "end": v(11.12, -6.31) * mm});
            skLineSegment(sketch, "E509", {"start": v(11.12, -6.31) * mm, "end": v(9.69, -6.3) * mm});
            skLineSegment(sketch, "E510", {"start": v(9.69, -6.3) * mm, "end": v(6.64, -6.3) * mm});
            skLineSegment(sketch, "E511", {"start": v(6.64, -6.3) * mm, "end": v(6.26, -6.3) * mm});
            skLineSegment(sketch, "E512", {"start": v(6.26, -6.3) * mm, "end": v(5.3, -6.33) * mm});
            skLineSegment(sketch, "E513", {"start": v(5.3, -6.33) * mm, "end": v(5.11, -6.33) * mm});
            skLineSegment(sketch, "E514", {"start": v(5.11, -6.33) * mm, "end": v(4.98, -6.33) * mm});
            skLineSegment(sketch, "E515", {"start": v(4.98, -6.33) * mm, "end": v(4.65, -6.37) * mm});
            skLineSegment(sketch, "E516", {"start": v(4.65, -6.37) * mm, "end": v(4.6, -6.37) * mm});
            skLineSegment(sketch, "E517", {"start": v(4.6, -6.37) * mm, "end": v(4.53, -6.38) * mm});
            skLineSegment(sketch, "E518", {"start": v(4.53, -6.38) * mm, "end": v(4.14, -6.4) * mm});
            skLineSegment(sketch, "E519", {"start": v(4.14, -6.4) * mm, "end": v(4, -6.4) * mm});
            skLineSegment(sketch, "E520", {"start": v(4, -6.4) * mm, "end": v(3.86, -6.4) * mm});
            skLineSegment(sketch, "E521", {"start": v(3.86, -6.4) * mm, "end": v(3.4, -6.24) * mm});
            skLineSegment(sketch, "E522", {"start": v(3.4, -6.24) * mm, "end": v(3.21, -5.85) * mm});
            skLineSegment(sketch, "E523", {"start": v(3.21, -5.85) * mm, "end": v(3.21, -5.73) * mm});
            skLineSegment(sketch, "E524", {"start": v(3.21, -5.73) * mm, "end": v(3.21, -5.6) * mm});
            skLineSegment(sketch, "E525", {"start": v(3.21, -5.6) * mm, "end": v(3.36, -5.27) * mm});
            skLineSegment(sketch, "E526", {"start": v(3.36, -5.27) * mm, "end": v(3.69, -5.11) * mm});
            skLineSegment(sketch, "E527", {"start": v(3.69, -5.11) * mm, "end": v(3.8, -5.11) * mm});
            skLineSegment(sketch, "E528", {"start": v(3.8, -5.11) * mm, "end": v(3.91, -5.11) * mm});
            skLineSegment(sketch, "E529", {"start": v(3.91, -5.11) * mm, "end": v(4.2, -5.15) * mm});
            skLineSegment(sketch, "E530", {"start": v(4.2, -5.15) * mm, "end": v(4.26, -5.16) * mm});
            skLineSegment(sketch, "E531", {"start": v(4.26, -5.16) * mm, "end": v(4.3, -5.17) * mm});
            skLineSegment(sketch, "E532", {"start": v(4.3, -5.17) * mm, "end": v(4.72, -5.2) * mm});
            skLineSegment(sketch, "E533", {"start": v(4.72, -5.2) * mm, "end": v(4.9, -5.2) * mm});
            skLineSegment(sketch, "E534", {"start": v(4.9, -5.2) * mm, "end": v(5.44, -4.85) * mm});
            skLineSegment(sketch, "E535", {"start": v(5.44, -4.85) * mm, "end": v(5.69, -4.05) * mm});
            skLineSegment(sketch, "E536", {"start": v(5.69, -4.05) * mm, "end": v(5.69, -3.78) * mm});
            skLineSegment(sketch, "E537", {"start": v(5.69, -3.78) * mm, "end": v(5.69, 3.86) * mm});
            skLineSegment(sketch, "E538", {"start": v(5.69, 3.86) * mm, "end": v(5.69, 4.12) * mm});
            skLineSegment(sketch, "E539", {"start": v(5.69, 4.12) * mm, "end": v(5.44, 4.92) * mm});
            skLineSegment(sketch, "E540", {"start": v(5.44, 4.92) * mm, "end": v(4.9, 5.27) * mm});
            skLineSegment(sketch, "E541", {"start": v(4.9, 5.27) * mm, "end": v(4.72, 5.27) * mm});
            skLineSegment(sketch, "E542", {"start": v(4.72, 5.27) * mm, "end": v(4.61, 5.27) * mm});
            skLineSegment(sketch, "E543", {"start": v(4.61, 5.27) * mm, "end": v(4.34, 5.24) * mm});
            skLineSegment(sketch, "E544", {"start": v(4.34, 5.24) * mm, "end": v(4.32, 5.23) * mm});
            skLineSegment(sketch, "E545", {"start": v(4.32, 5.23) * mm, "end": v(4.26, 5.22) * mm});
            skLineSegment(sketch, "E546", {"start": v(4.26, 5.22) * mm, "end": v(3.92, 5.17) * mm});
            skLineSegment(sketch, "E547", {"start": v(3.92, 5.17) * mm, "end": v(3.8, 5.17) * mm});
            skLineSegment(sketch, "E548", {"start": v(3.8, 5.17) * mm, "end": v(3.7, 5.17) * mm});
            skLineSegment(sketch, "E549", {"start": v(3.7, 5.17) * mm, "end": v(3.4, 5.32) * mm});
            skLineSegment(sketch, "E550", {"start": v(3.4, 5.32) * mm, "end": v(3.38, 5.35) * mm});
            skLineSegment(sketch, "E551", {"start": v(3.38, 5.35) * mm, "end": v(3.35, 5.38) * mm});
            skLineSegment(sketch, "E552", {"start": v(3.35, 5.38) * mm, "end": v(3.21, 5.7) * mm});
            skLineSegment(sketch, "E553", {"start": v(3.21, 5.7) * mm, "end": v(3.21, 5.8) * mm});
            skLineSegment(sketch, "E554", {"start": v(3.21, 5.8) * mm, "end": v(3.21, 5.93) * mm});
            skLineSegment(sketch, "E555", {"start": v(3.21, 5.93) * mm, "end": v(3.41, 6.3) * mm});
            skLineSegment(sketch, "E556", {"start": v(3.41, 6.3) * mm, "end": v(3.87, 6.47) * mm});
            skLineSegment(sketch, "E557", {"start": v(3.87, 6.47) * mm, "end": v(4.03, 6.47) * mm});
            skLineSegment(sketch, "E558", {"start": v(4.03, 6.47) * mm, "end": v(4.1, 6.47) * mm});
            skLineSegment(sketch, "E559", {"start": v(4.1, 6.47) * mm, "end": v(4.29, 6.45) * mm});
            skLineSegment(sketch, "E560", {"start": v(4.29, 6.45) * mm, "end": v(4.32, 6.45) * mm});
            skLineSegment(sketch, "E561", {"start": v(4.32, 6.45) * mm, "end": v(5.32, 6.33) * mm});
            skLineSegment(sketch, "E562", {"start": v(5.32, 6.33) * mm, "end": v(5.46, 6.32) * mm});
            skLineSegment(sketch, "E563", {"start": v(5.46, 6.32) * mm, "end": v(6.29, 6.24) * mm});
            skLineSegment(sketch, "E564", {"start": v(6.29, 6.24) * mm, "end": v(6.56, 6.24) * mm});
            skLineSegment(sketch, "E565", {"start": v(6.56, 6.24) * mm, "end": v(6.87, 6.24) * mm});
            skLineSegment(sketch, "E566", {"start": v(6.87, 6.24) * mm, "end": v(7.66, 6.32) * mm});
            skLineSegment(sketch, "E567", {"start": v(7.66, 6.32) * mm, "end": v(7.78, 6.33) * mm});
            skLineSegment(sketch, "E568", {"start": v(7.78, 6.33) * mm, "end": v(8.66, 6.45) * mm});
            skLineSegment(sketch, "E569", {"start": v(8.66, 6.45) * mm, "end": v(8.68, 6.45) * mm});
            skLineSegment(sketch, "E570", {"start": v(8.68, 6.45) * mm, "end": v(8.85, 6.47) * mm});
            skLineSegment(sketch, "E571", {"start": v(8.85, 6.47) * mm, "end": v(8.9, 6.47) * mm});
            skLineSegment(sketch, "E572", {"start": v(8.9, 6.47) * mm, "end": v(9.07, 6.47) * mm});
            skLineSegment(sketch, "E573", {"start": v(9.07, 6.47) * mm, "end": v(9.55, 6.3) * mm});
            skLineSegment(sketch, "E574", {"start": v(9.55, 6.3) * mm, "end": v(9.76, 5.93) * mm});
            skLineSegment(sketch, "E575", {"start": v(9.76, 5.93) * mm, "end": v(9.76, 5.8) * mm});
            skLineSegment(sketch, "E576", {"start": v(9.76, 5.8) * mm, "end": v(9.76, 5.69) * mm});
            skLineSegment(sketch, "E577", {"start": v(9.76, 5.69) * mm, "end": v(9.62, 5.38) * mm});
            skLineSegment(sketch, "E578", {"start": v(9.62, 5.38) * mm, "end": v(9.6, 5.35) * mm});
            skLineSegment(sketch, "E579", {"start": v(9.6, 5.35) * mm, "end": v(9.56, 5.32) * mm});
            skLineSegment(sketch, "E580", {"start": v(9.56, 5.32) * mm, "end": v(9.27, 5.17) * mm});
            skLineSegment(sketch, "E581", {"start": v(9.27, 5.17) * mm, "end": v(9.17, 5.17) * mm});
            skLineSegment(sketch, "E582", {"start": v(9.17, 5.17) * mm, "end": v(9.04, 5.17) * mm});
            skLineSegment(sketch, "E583", {"start": v(9.04, 5.17) * mm, "end": v(8.71, 5.22) * mm});
            skLineSegment(sketch, "E584", {"start": v(8.71, 5.22) * mm, "end": v(8.66, 5.23) * mm});
            skLineSegment(sketch, "E585", {"start": v(8.66, 5.23) * mm, "end": v(8.64, 5.24) * mm});
            skLineSegment(sketch, "E586", {"start": v(8.64, 5.24) * mm, "end": v(8.35, 5.27) * mm});
            skLineSegment(sketch, "E587", {"start": v(8.35, 5.27) * mm, "end": v(8.26, 5.27) * mm});
            skLineSegment(sketch, "E588", {"start": v(8.26, 5.27) * mm, "end": v(8.07, 5.27) * mm});
            skLineSegment(sketch, "E589", {"start": v(8.07, 5.27) * mm, "end": v(7.53, 4.92) * mm});
            skLineSegment(sketch, "E590", {"start": v(7.53, 4.92) * mm, "end": v(7.29, 4.12) * mm});
            skLineSegment(sketch, "E591", {"start": v(7.29, 4.12) * mm, "end": v(7.29, 3.86) * mm});
            skLineSegment(sketch, "E592", {"start": v(7.29, 3.86) * mm, "end": v(7.29, -3.57) * mm});
            skLineSegment(sketch, "E593", {"start": v(23.92, -6.56) * mm, "end": v(23.6, -6.56) * mm});
            skLineSegment(sketch, "E594", {"start": v(23.6, -6.56) * mm, "end": v(22.65, -6.22) * mm});
            skLineSegment(sketch, "E595", {"start": v(22.65, -6.22) * mm, "end": v(22.05, -5.43) * mm});
            skLineSegment(sketch, "E596", {"start": v(22.05, -5.43) * mm, "end": v(22, -5.2) * mm});
            skLineSegment(sketch, "E597", {"start": v(22, -5.2) * mm, "end": v(21.83, -5.45) * mm});
            skLineSegment(sketch, "E598", {"start": v(21.83, -5.45) * mm, "end": v(20.74, -6.28) * mm});
            skLineSegment(sketch, "E599", {"start": v(20.74, -6.28) * mm, "end": v(19.4, -6.64) * mm});
            skLineSegment(sketch, "E600", {"start": v(19.4, -6.64) * mm, "end": v(18.94, -6.64) * mm});
            skLineSegment(sketch, "E601", {"start": v(18.94, -6.64) * mm, "end": v(18.6, -6.64) * mm});
            skLineSegment(sketch, "E602", {"start": v(18.6, -6.64) * mm, "end": v(17.56, -6.45) * mm});
            skLineSegment(sketch, "E603", {"start": v(17.56, -6.45) * mm, "end": v(16.63, -6) * mm});
            skLineSegment(sketch, "E604", {"start": v(16.63, -6) * mm, "end": v(16.48, -5.88) * mm});
            skLineSegment(sketch, "E605", {"start": v(16.48, -5.88) * mm, "end": v(16.32, -5.75) * mm});
            skLineSegment(sketch, "E606", {"start": v(16.32, -5.75) * mm, "end": v(15.78, -4.99) * mm});
            skLineSegment(sketch, "E607", {"start": v(15.78, -4.99) * mm, "end": v(15.55, -4.13) * mm});
            skLineSegment(sketch, "E608", {"start": v(15.55, -4.13) * mm, "end": v(15.55, -3.84) * mm});
            skLineSegment(sketch, "E609", {"start": v(15.55, -3.84) * mm, "end": v(15.55, -3.5) * mm});
            skLineSegment(sketch, "E610", {"start": v(15.55, -3.5) * mm, "end": v(15.9, -2.47) * mm});
            skLineSegment(sketch, "E611", {"start": v(15.9, -2.47) * mm, "end": v(16.68, -1.64) * mm});
            skLineSegment(sketch, "E612", {"start": v(16.68, -1.64) * mm, "end": v(16.9, -1.52) * mm});
            skLineSegment(sketch, "E613", {"start": v(16.9, -1.52) * mm, "end": v(17, -1.47) * mm});
            skLineSegment(sketch, "E614", {"start": v(17, -1.47) * mm, "end": v(17.73, -1.16) * mm});
            skLineSegment(sketch, "E615", {"start": v(17.73, -1.16) * mm, "end": v(17.8, -1.14) * mm});
            skLineSegment(sketch, "E616", {"start": v(17.8, -1.14) * mm, "end": v(17.85, -1.13) * mm});
            skLineSegment(sketch, "E617", {"start": v(17.85, -1.13) * mm, "end": v(18.35, -1.05) * mm});
            skLineSegment(sketch, "E618", {"start": v(18.35, -1.05) * mm, "end": v(19.1, -0.95) * mm});
            skLineSegment(sketch, "E619", {"start": v(19.1, -0.95) * mm, "end": v(19.29, -0.92) * mm});
            skLineSegment(sketch, "E620", {"start": v(19.29, -0.92) * mm, "end": v(19.55, -0.9) * mm});
            skLineSegment(sketch, "E621", {"start": v(19.55, -0.9) * mm, "end": v(20.6, -0.72) * mm});
            skLineSegment(sketch, "E622", {"start": v(20.6, -0.72) * mm, "end": v(21.3, -0.5) * mm});
            skLineSegment(sketch, "E623", {"start": v(21.3, -0.5) * mm, "end": v(21.37, -0.45) * mm});
            skLineSegment(sketch, "E624", {"start": v(21.37, -0.45) * mm, "end": v(21.45, -0.4) * mm});
            skLineSegment(sketch, "E625", {"start": v(21.45, -0.4) * mm, "end": v(21.74, -0.01) * mm});
            skLineSegment(sketch, "E626", {"start": v(21.74, -0.01) * mm, "end": v(21.86, 0.5) * mm});
            skLineSegment(sketch, "E627", {"start": v(21.86, 0.5) * mm, "end": v(21.86, 0.68) * mm});
            skLineSegment(sketch, "E628", {"start": v(21.86, 0.68) * mm, "end": v(21.86, 0.85) * mm});
            skLineSegment(sketch, "E629", {"start": v(21.86, 0.85) * mm, "end": v(21.72, 1.37) * mm});
            skLineSegment(sketch, "E630", {"start": v(21.72, 1.37) * mm, "end": v(21.4, 1.83) * mm});
            skLineSegment(sketch, "E631", {"start": v(21.4, 1.83) * mm, "end": v(21.32, 1.9) * mm});
            skLineSegment(sketch, "E632", {"start": v(21.32, 1.9) * mm, "end": v(21.23, 1.98) * mm});
            skLineSegment(sketch, "E633", {"start": v(21.23, 1.98) * mm, "end": v(20.67, 2.24) * mm});
            skLineSegment(sketch, "E634", {"start": v(20.67, 2.24) * mm, "end": v(20.02, 2.35) * mm});
            skLineSegment(sketch, "E635", {"start": v(20.02, 2.35) * mm, "end": v(19.8, 2.35) * mm});
            skLineSegment(sketch, "E636", {"start": v(19.8, 2.35) * mm, "end": v(19.4, 2.35) * mm});
            skLineSegment(sketch, "E637", {"start": v(19.4, 2.35) * mm, "end": v(18.33, 1.96) * mm});
            skLineSegment(sketch, "E638", {"start": v(18.33, 1.96) * mm, "end": v(18.2, 1.88) * mm});
            skLineSegment(sketch, "E639", {"start": v(18.2, 1.88) * mm, "end": v(18.15, 1.84) * mm});
            skLineSegment(sketch, "E640", {"start": v(18.15, 1.84) * mm, "end": v(17.92, 1.57) * mm});
            skLineSegment(sketch, "E641", {"start": v(17.92, 1.57) * mm, "end": v(17.92, 1.48) * mm});
            skLineSegment(sketch, "E642", {"start": v(17.92, 1.48) * mm, "end": v(17.92, 1.43) * mm});
            skLineSegment(sketch, "E643", {"start": v(17.92, 1.43) * mm, "end": v(18.06, 1.3) * mm});
            skLineSegment(sketch, "E644", {"start": v(18.06, 1.3) * mm, "end": v(18.09, 1.29) * mm});
            skLineSegment(sketch, "E645", {"start": v(18.09, 1.29) * mm, "end": v(18.13, 1.25) * mm});
            skLineSegment(sketch, "E646", {"start": v(18.13, 1.25) * mm, "end": v(18.35, 0.8) * mm});
            skLineSegment(sketch, "E647", {"start": v(18.35, 0.8) * mm, "end": v(18.35, 0.64) * mm});
            skLineSegment(sketch, "E648", {"start": v(18.35, 0.64) * mm, "end": v(18.35, 0.48) * mm});
            skLineSegment(sketch, "E649", {"start": v(18.35, 0.48) * mm, "end": v(18.12, 0.05) * mm});
            skLineSegment(sketch, "E650", {"start": v(18.12, 0.05) * mm, "end": v(18.08, 0) * mm});
            skLineSegment(sketch, "E651", {"start": v(18.08, 0) * mm, "end": v(18.03, -0.03) * mm});
            skLineSegment(sketch, "E652", {"start": v(18.03, -0.03) * mm, "end": v(17.54, -0.24) * mm});
            skLineSegment(sketch, "E653", {"start": v(17.54, -0.24) * mm, "end": v(17.38, -0.24) * mm});
            skLineSegment(sketch, "E654", {"start": v(17.38, -0.24) * mm, "end": v(17.18, -0.24) * mm});
            skLineSegment(sketch, "E655", {"start": v(17.18, -0.24) * mm, "end": v(16.61, 0.05) * mm});
            skLineSegment(sketch, "E656", {"start": v(16.61, 0.05) * mm, "end": v(16.56, 0.1) * mm});
            skLineSegment(sketch, "E657", {"start": v(16.56, 0.1) * mm, "end": v(16.5, 0.16) * mm});
            skLineSegment(sketch, "E658", {"start": v(16.5, 0.16) * mm, "end": v(16.22, 0.75) * mm});
            skLineSegment(sketch, "E659", {"start": v(16.22, 0.75) * mm, "end": v(16.22, 0.94) * mm});
            skLineSegment(sketch, "E660", {"start": v(16.22, 0.94) * mm, "end": v(16.22, 1.2) * mm});
            skLineSegment(sketch, "E661", {"start": v(16.22, 1.2) * mm, "end": v(16.49, 1.93) * mm});
            skLineSegment(sketch, "E662", {"start": v(16.49, 1.93) * mm, "end": v(17.1, 2.65) * mm});
            skLineSegment(sketch, "E663", {"start": v(17.1, 2.65) * mm, "end": v(17.28, 2.77) * mm});
            skLineSegment(sketch, "E664", {"start": v(17.28, 2.77) * mm, "end": v(17.45, 2.9) * mm});
            skLineSegment(sketch, "E665", {"start": v(17.45, 2.9) * mm, "end": v(18.45, 3.34) * mm});
            skLineSegment(sketch, "E666", {"start": v(18.45, 3.34) * mm, "end": v(19.5, 3.53) * mm});
            skLineSegment(sketch, "E667", {"start": v(19.5, 3.53) * mm, "end": v(19.84, 3.53) * mm});
            skLineSegment(sketch, "E668", {"start": v(19.84, 3.53) * mm, "end": v(20.22, 3.53) * mm});
            skLineSegment(sketch, "E669", {"start": v(20.22, 3.53) * mm, "end": v(21.36, 3.33) * mm});
            skLineSegment(sketch, "E670", {"start": v(21.36, 3.33) * mm, "end": v(22.44, 2.7) * mm});
            skLineSegment(sketch, "E671", {"start": v(22.44, 2.7) * mm, "end": v(23.09, 1.66) * mm});
            skLineSegment(sketch, "E672", {"start": v(23.09, 1.66) * mm, "end": v(23.3, 0.57) * mm});
            skLineSegment(sketch, "E673", {"start": v(23.3, 0.57) * mm, "end": v(23.3, 0.2) * mm});
            skLineSegment(sketch, "E674", {"start": v(23.3, 0.2) * mm, "end": v(23.3, -3.65) * mm});
            skLineSegment(sketch, "E675", {"start": v(23.3, -3.65) * mm, "end": v(23.3, -3.83) * mm});
            skLineSegment(sketch, "E676", {"start": v(23.3, -3.83) * mm, "end": v(23.32, -4.38) * mm});
            skLineSegment(sketch, "E677", {"start": v(23.32, -4.38) * mm, "end": v(23.34, -4.7) * mm});
            skLineSegment(sketch, "E678", {"start": v(23.34, -4.7) * mm, "end": v(23.35, -4.73) * mm});
            skLineSegment(sketch, "E679", {"start": v(23.35, -4.73) * mm, "end": v(23.36, -4.84) * mm});
            skLineSegment(sketch, "E680", {"start": v(23.36, -4.84) * mm, "end": v(23.56, -5.23) * mm});
            skLineSegment(sketch, "E681", {"start": v(23.56, -5.23) * mm, "end": v(23.89, -5.4) * mm});
            skLineSegment(sketch, "E682", {"start": v(23.89, -5.4) * mm, "end": v(24, -5.4) * mm});
            skLineSegment(sketch, "E683", {"start": v(24, -5.4) * mm, "end": v(24.12, -5.4) * mm});
            skLineSegment(sketch, "E684", {"start": v(24.12, -5.4) * mm, "end": v(24.5, -5.1) * mm});
            skLineSegment(sketch, "E685", {"start": v(24.5, -5.1) * mm, "end": v(24.66, -4.4) * mm});
            skLineSegment(sketch, "E686", {"start": v(24.66, -4.4) * mm, "end": v(24.66, -4.18) * mm});
            skLineSegment(sketch, "E687", {"start": v(24.66, -4.18) * mm, "end": v(24.66, -3.25) * mm});
            skLineSegment(sketch, "E688", {"start": v(24.66, -3.25) * mm, "end": v(24.66, -3.13) * mm});
            skLineSegment(sketch, "E689", {"start": v(24.66, -3.13) * mm, "end": v(24.8, -2.79) * mm});
            skLineSegment(sketch, "E690", {"start": v(24.8, -2.79) * mm, "end": v(25.14, -2.64) * mm});
            skLineSegment(sketch, "E691", {"start": v(25.14, -2.64) * mm, "end": v(25.25, -2.64) * mm});
            skLineSegment(sketch, "E692", {"start": v(25.25, -2.64) * mm, "end": v(25.37, -2.64) * mm});
            skLineSegment(sketch, "E693", {"start": v(25.37, -2.64) * mm, "end": v(25.72, -2.87) * mm});
            skLineSegment(sketch, "E694", {"start": v(25.72, -2.87) * mm, "end": v(25.88, -3.38) * mm});
            skLineSegment(sketch, "E695", {"start": v(25.88, -3.38) * mm, "end": v(25.88, -3.55) * mm});
            skLineSegment(sketch, "E696", {"start": v(25.88, -3.55) * mm, "end": v(25.88, -3.65) * mm});
            skLineSegment(sketch, "E697", {"start": v(25.88, -3.65) * mm, "end": v(25.86, -4.73) * mm});
            skLineSegment(sketch, "E698", {"start": v(25.86, -4.73) * mm, "end": v(25.86, -4.93) * mm});
            skLineSegment(sketch, "E699", {"start": v(25.86, -4.93) * mm, "end": v(25.72, -5.53) * mm});
            skLineSegment(sketch, "E700", {"start": v(25.72, -5.53) * mm, "end": v(25.36, -6.1) * mm});
            skLineSegment(sketch, "E701", {"start": v(25.36, -6.1) * mm, "end": v(24.75, -6.45) * mm});
            skLineSegment(sketch, "E702", {"start": v(24.75, -6.45) * mm, "end": v(24.12, -6.56) * mm});
            skLineSegment(sketch, "E703", {"start": v(24.12, -6.56) * mm, "end": v(23.92, -6.56) * mm});
            skLineSegment(sketch, "E704", {"start": v(21.8, -2.77) * mm, "end": v(21.82, -1.42) * mm});
            skLineSegment(sketch, "E705", {"start": v(21.82, -1.42) * mm, "end": v(21.75, -1.48) * mm});
            skLineSegment(sketch, "E706", {"start": v(21.75, -1.48) * mm, "end": v(21.01, -1.93) * mm});
            skLineSegment(sketch, "E707", {"start": v(21.01, -1.93) * mm, "end": v(20.94, -1.95) * mm});
            skLineSegment(sketch, "E708", {"start": v(20.94, -1.95) * mm, "end": v(20.86, -1.98) * mm});
            skLineSegment(sketch, "E709", {"start": v(20.86, -1.98) * mm, "end": v(20.29, -2.1) * mm});
            skLineSegment(sketch, "E710", {"start": v(20.29, -2.1) * mm, "end": v(19.47, -2.2) * mm});
            skLineSegment(sketch, "E711", {"start": v(19.47, -2.2) * mm, "end": v(19.27, -2.22) * mm});
            skLineSegment(sketch, "E712", {"start": v(19.27, -2.22) * mm, "end": v(19.03, -2.24) * mm});
            skLineSegment(sketch, "E713", {"start": v(19.03, -2.24) * mm, "end": v(18.32, -2.4) * mm});
            skLineSegment(sketch, "E714", {"start": v(18.32, -2.4) * mm, "end": v(17.64, -2.72) * mm});
            skLineSegment(sketch, "E715", {"start": v(17.64, -2.72) * mm, "end": v(17.23, -3.2) * mm});
            skLineSegment(sketch, "E716", {"start": v(17.23, -3.2) * mm, "end": v(17.1, -3.66) * mm});
            skLineSegment(sketch, "E717", {"start": v(17.1, -3.66) * mm, "end": v(17.1, -3.82) * mm});
            skLineSegment(sketch, "E718", {"start": v(17.1, -3.82) * mm, "end": v(17.1, -3.98) * mm});
            skLineSegment(sketch, "E719", {"start": v(17.1, -3.98) * mm, "end": v(17.23, -4.47) * mm});
            skLineSegment(sketch, "E720", {"start": v(17.23, -4.47) * mm, "end": v(17.53, -4.9) * mm});
            skLineSegment(sketch, "E721", {"start": v(17.53, -4.9) * mm, "end": v(17.62, -4.96) * mm});
            skLineSegment(sketch, "E722", {"start": v(17.62, -4.96) * mm, "end": v(17.7, -5.03) * mm});
            skLineSegment(sketch, "E723", {"start": v(17.7, -5.03) * mm, "end": v(18.24, -5.28) * mm});
            skLineSegment(sketch, "E724", {"start": v(18.24, -5.28) * mm, "end": v(18.84, -5.38) * mm});
            skLineSegment(sketch, "E725", {"start": v(18.84, -5.38) * mm, "end": v(19.04, -5.38) * mm});
            skLineSegment(sketch, "E726", {"start": v(19.04, -5.38) * mm, "end": v(19.32, -5.38) * mm});
            skLineSegment(sketch, "E727", {"start": v(19.32, -5.38) * mm, "end": v(20.18, -5.2) * mm});
            skLineSegment(sketch, "E728", {"start": v(20.18, -5.2) * mm, "end": v(20.93, -4.8) * mm});
            skLineSegment(sketch, "E729", {"start": v(20.93, -4.8) * mm, "end": v(21.05, -4.69) * mm});
            skLineSegment(sketch, "E730", {"start": v(21.05, -4.69) * mm, "end": v(21.17, -4.57) * mm});
            skLineSegment(sketch, "E731", {"start": v(21.17, -4.57) * mm, "end": v(21.6, -3.86) * mm});
            skLineSegment(sketch, "E732", {"start": v(21.6, -3.86) * mm, "end": v(21.8, -2.97) * mm});
            skLineSegment(sketch, "E733", {"start": v(21.8, -2.97) * mm, "end": v(21.8, -2.77) * mm});
            skLineSegment(sketch, "E734", {"start": v(28.95, 5.84) * mm, "end": v(28.92, 5.57) * mm});
            skLineSegment(sketch, "E735", {"start": v(28.92, 5.57) * mm, "end": v(28.83, 4.1) * mm});
            skLineSegment(sketch, "E736", {"start": v(28.83, 4.1) * mm, "end": v(28.78, 2.45) * mm});
            skLineSegment(sketch, "E737", {"start": v(28.78, 2.45) * mm, "end": v(28.78, 2.09) * mm});
            skLineSegment(sketch, "E738", {"start": v(28.78, 2.09) * mm, "end": v(28.88, 2.22) * mm});
            skLineSegment(sketch, "E739", {"start": v(28.88, 2.22) * mm, "end": v(29.9, 3.16) * mm});
            skLineSegment(sketch, "E740", {"start": v(29.9, 3.16) * mm, "end": v(30.01, 3.21) * mm});
            skLineSegment(sketch, "E741", {"start": v(30.01, 3.21) * mm, "end": v(30.12, 3.26) * mm});
            skLineSegment(sketch, "E742", {"start": v(30.12, 3.26) * mm, "end": v(31.22, 3.53) * mm});
            skLineSegment(sketch, "E743", {"start": v(31.22, 3.53) * mm, "end": v(31.6, 3.53) * mm});
            skLineSegment(sketch, "E744", {"start": v(31.6, 3.53) * mm, "end": v(32.02, 3.53) * mm});
            skLineSegment(sketch, "E745", {"start": v(32.02, 3.53) * mm, "end": v(33.3, 3.2) * mm});
            skLineSegment(sketch, "E746", {"start": v(33.3, 3.2) * mm, "end": v(34.44, 2.42) * mm});
            skLineSegment(sketch, "E747", {"start": v(34.44, 2.42) * mm, "end": v(34.62, 2.2) * mm});
            skLineSegment(sketch, "E748", {"start": v(34.62, 2.2) * mm, "end": v(34.8, 1.98) * mm});
            skLineSegment(sketch, "E749", {"start": v(34.8, 1.98) * mm, "end": v(35.47, 0.65) * mm});
            skLineSegment(sketch, "E750", {"start": v(35.47, 0.65) * mm, "end": v(35.75, -0.84) * mm});
            skLineSegment(sketch, "E751", {"start": v(35.75, -0.84) * mm, "end": v(35.75, -1.34) * mm});
            skLineSegment(sketch, "E752", {"start": v(35.75, -1.34) * mm, "end": v(35.75, -1.89) * mm});
            skLineSegment(sketch, "E753", {"start": v(35.75, -1.89) * mm, "end": v(35.45, -3.52) * mm});
            skLineSegment(sketch, "E754", {"start": v(35.45, -3.52) * mm, "end": v(34.76, -4.96) * mm});
            skLineSegment(sketch, "E755", {"start": v(34.76, -4.96) * mm, "end": v(34.56, -5.2) * mm});
            skLineSegment(sketch, "E756", {"start": v(34.56, -5.2) * mm, "end": v(34.36, -5.44) * mm});
            skLineSegment(sketch, "E757", {"start": v(34.36, -5.44) * mm, "end": v(33.16, -6.28) * mm});
            skLineSegment(sketch, "E758", {"start": v(33.16, -6.28) * mm, "end": v(31.8, -6.64) * mm});
            skLineSegment(sketch, "E759", {"start": v(31.8, -6.64) * mm, "end": v(31.35, -6.64) * mm});
            skLineSegment(sketch, "E760", {"start": v(31.35, -6.64) * mm, "end": v(30.92, -6.64) * mm});
            skLineSegment(sketch, "E761", {"start": v(30.92, -6.64) * mm, "end": v(29.66, -6.27) * mm});
            skLineSegment(sketch, "E762", {"start": v(29.66, -6.27) * mm, "end": v(28.65, -5.42) * mm});
            skLineSegment(sketch, "E763", {"start": v(28.65, -5.42) * mm, "end": v(28.5, -5.17) * mm});
            skLineSegment(sketch, "E764", {"start": v(28.5, -5.17) * mm, "end": v(28.52, -5.26) * mm});
            skLineSegment(sketch, "E765", {"start": v(28.52, -5.26) * mm, "end": v(28.58, -5.65) * mm});
            skLineSegment(sketch, "E766", {"start": v(28.58, -5.65) * mm, "end": v(28.58, -5.78) * mm});
            skLineSegment(sketch, "E767", {"start": v(28.58, -5.78) * mm, "end": v(28.58, -5.9) * mm});
            skLineSegment(sketch, "E768", {"start": v(28.58, -5.9) * mm, "end": v(28.42, -6.3) * mm});
            skLineSegment(sketch, "E769", {"start": v(28.42, -6.3) * mm, "end": v(28.04, -6.47) * mm});
            skLineSegment(sketch, "E770", {"start": v(28.04, -6.47) * mm, "end": v(27.92, -6.47) * mm});
            skLineSegment(sketch, "E771", {"start": v(27.92, -6.47) * mm, "end": v(27.8, -6.47) * mm});
            skLineSegment(sketch, "E772", {"start": v(27.8, -6.47) * mm, "end": v(27.42, -6.23) * mm});
            skLineSegment(sketch, "E773", {"start": v(27.42, -6.23) * mm, "end": v(27.25, -5.7) * mm});
            skLineSegment(sketch, "E774", {"start": v(27.25, -5.7) * mm, "end": v(27.25, -5.52) * mm});
            skLineSegment(sketch, "E775", {"start": v(27.25, -5.52) * mm, "end": v(27.25, -5.42) * mm});
            skLineSegment(sketch, "E776", {"start": v(27.25, -5.42) * mm, "end": v(27.27, -5.14) * mm});
            skLineSegment(sketch, "E777", {"start": v(27.27, -5.14) * mm, "end": v(27.27, -5.11) * mm});
            skLineSegment(sketch, "E778", {"start": v(27.27, -5.11) * mm, "end": v(27.27, -4.88) * mm});
            skLineSegment(sketch, "E779", {"start": v(27.27, -4.88) * mm, "end": v(27.28, -4.26) * mm});
            skLineSegment(sketch, "E780", {"start": v(27.28, -4.26) * mm, "end": v(27.29, -4.18) * mm});
            skLineSegment(sketch, "E781", {"start": v(27.29, -4.18) * mm, "end": v(27.35, -2.72) * mm});
            skLineSegment(sketch, "E782", {"start": v(27.35, -2.72) * mm, "end": v(27.38, -0.8) * mm});
            skLineSegment(sketch, "E783", {"start": v(27.38, -0.8) * mm, "end": v(27.35, 4.3) * mm});
            skLineSegment(sketch, "E784", {"start": v(27.35, 4.3) * mm, "end": v(27.34, 4.41) * mm});
            skLineSegment(sketch, "E785", {"start": v(27.34, 4.41) * mm, "end": v(27.22, 5.2) * mm});
            skLineSegment(sketch, "E786", {"start": v(27.22, 5.2) * mm, "end": v(27.2, 5.25) * mm});
            skLineSegment(sketch, "E787", {"start": v(27.2, 5.25) * mm, "end": v(27.18, 5.29) * mm});
            skLineSegment(sketch, "E788", {"start": v(27.18, 5.29) * mm, "end": v(26.88, 5.5) * mm});
            skLineSegment(sketch, "E789", {"start": v(26.88, 5.5) * mm, "end": v(26.77, 5.5) * mm});
            skLineSegment(sketch, "E790", {"start": v(26.77, 5.5) * mm, "end": v(26.65, 5.5) * mm});
            skLineSegment(sketch, "E791", {"start": v(26.65, 5.5) * mm, "end": v(26.35, 5.43) * mm});
            skLineSegment(sketch, "E792", {"start": v(26.35, 5.43) * mm, "end": v(26.28, 5.42) * mm});
            skLineSegment(sketch, "E793", {"start": v(26.28, 5.42) * mm, "end": v(26.24, 5.41) * mm});
            skLineSegment(sketch, "E794", {"start": v(26.24, 5.41) * mm, "end": v(26, 5.38) * mm});
            skLineSegment(sketch, "E795", {"start": v(26, 5.38) * mm, "end": v(25.92, 5.38) * mm});
            skLineSegment(sketch, "E796", {"start": v(25.92, 5.38) * mm, "end": v(25.8, 5.38) * mm});
            skLineSegment(sketch, "E797", {"start": v(25.8, 5.38) * mm, "end": v(25.43, 5.53) * mm});
            skLineSegment(sketch, "E798", {"start": v(25.43, 5.53) * mm, "end": v(25.27, 5.88) * mm});
            skLineSegment(sketch, "E799", {"start": v(25.27, 5.88) * mm, "end": v(25.27, 6) * mm});
            skLineSegment(sketch, "E800", {"start": v(25.27, 6) * mm, "end": v(25.27, 6.1) * mm});
            skLineSegment(sketch, "E801", {"start": v(25.27, 6.1) * mm, "end": v(25.46, 6.46) * mm});
            skLineSegment(sketch, "E802", {"start": v(25.46, 6.46) * mm, "end": v(25.89, 6.62) * mm});
            skLineSegment(sketch, "E803", {"start": v(25.89, 6.62) * mm, "end": v(26.03, 6.62) * mm});
            skLineSegment(sketch, "E804", {"start": v(26.03, 6.62) * mm, "end": v(26.13, 6.62) * mm});
            skLineSegment(sketch, "E805", {"start": v(26.13, 6.62) * mm, "end": v(26.39, 6.6) * mm});
            skLineSegment(sketch, "E806", {"start": v(26.39, 6.6) * mm, "end": v(26.41, 6.6) * mm});
            skLineSegment(sketch, "E807", {"start": v(26.41, 6.6) * mm, "end": v(26.87, 6.54) * mm});
            skLineSegment(sketch, "E808", {"start": v(26.87, 6.54) * mm, "end": v(26.92, 6.54) * mm});
            skLineSegment(sketch, "E809", {"start": v(26.92, 6.54) * mm, "end": v(27.25, 6.5) * mm});
            skLineSegment(sketch, "E810", {"start": v(27.25, 6.5) * mm, "end": v(27.37, 6.5) * mm});
            skLineSegment(sketch, "E811", {"start": v(27.37, 6.5) * mm, "end": v(27.51, 6.5) * mm});
            skLineSegment(sketch, "E812", {"start": v(27.51, 6.5) * mm, "end": v(27.9, 6.56) * mm});
            skLineSegment(sketch, "E813", {"start": v(27.9, 6.56) * mm, "end": v(27.96, 6.57) * mm});
            skLineSegment(sketch, "E814", {"start": v(27.96, 6.57) * mm, "end": v(28.02, 6.58) * mm});
            skLineSegment(sketch, "E815", {"start": v(28.02, 6.58) * mm, "end": v(28.4, 6.64) * mm});
            skLineSegment(sketch, "E816", {"start": v(28.4, 6.64) * mm, "end": v(28.53, 6.64) * mm});
            skLineSegment(sketch, "E817", {"start": v(28.53, 6.64) * mm, "end": v(28.6, 6.64) * mm});
            skLineSegment(sketch, "E818", {"start": v(28.6, 6.64) * mm, "end": v(28.84, 6.5) * mm});
            skLineSegment(sketch, "E819", {"start": v(28.84, 6.5) * mm, "end": v(28.95, 6.2) * mm});
            skLineSegment(sketch, "E820", {"start": v(28.95, 6.2) * mm, "end": v(28.95, 6.1) * mm});
            skLineSegment(sketch, "E821", {"start": v(28.95, 6.1) * mm, "end": v(28.95, 5.84) * mm});
            skLineSegment(sketch, "E822", {"start": v(28.93, 0.31) * mm, "end": v(28.9, 0.21) * mm});
            skLineSegment(sketch, "E823", {"start": v(28.9, 0.21) * mm, "end": v(28.8, -1) * mm});
            skLineSegment(sketch, "E824", {"start": v(28.8, -1) * mm, "end": v(28.8, -1.4) * mm});
            skLineSegment(sketch, "E825", {"start": v(28.8, -1.4) * mm, "end": v(28.8, -1.8) * mm});
            skLineSegment(sketch, "E826", {"start": v(28.8, -1.8) * mm, "end": v(28.87, -3) * mm});
            skLineSegment(sketch, "E827", {"start": v(28.87, -3) * mm, "end": v(29.05, -3.87) * mm});
            skLineSegment(sketch, "E828", {"start": v(29.05, -3.87) * mm, "end": v(29.1, -4) * mm});
            skLineSegment(sketch, "E829", {"start": v(29.1, -4) * mm, "end": v(29.2, -4.22) * mm});
            skLineSegment(sketch, "E830", {"start": v(29.2, -4.22) * mm, "end": v(29.95, -5.03) * mm});
            skLineSegment(sketch, "E831", {"start": v(29.95, -5.03) * mm, "end": v(31, -5.38) * mm});
            skLineSegment(sketch, "E832", {"start": v(31, -5.38) * mm, "end": v(31.35, -5.38) * mm});
            skLineSegment(sketch, "E833", {"start": v(31.35, -5.38) * mm, "end": v(31.64, -5.38) * mm});
            skLineSegment(sketch, "E834", {"start": v(31.64, -5.38) * mm, "end": v(32.52, -5.12) * mm});
            skLineSegment(sketch, "E835", {"start": v(32.52, -5.12) * mm, "end": v(33.3, -4.52) * mm});
            skLineSegment(sketch, "E836", {"start": v(33.3, -4.52) * mm, "end": v(33.43, -4.34) * mm});
            skLineSegment(sketch, "E837", {"start": v(33.43, -4.34) * mm, "end": v(33.56, -4.17) * mm});
            skLineSegment(sketch, "E838", {"start": v(33.56, -4.17) * mm, "end": v(34.01, -3.13) * mm});
            skLineSegment(sketch, "E839", {"start": v(34.01, -3.13) * mm, "end": v(34.2, -1.95) * mm});
            skLineSegment(sketch, "E840", {"start": v(34.2, -1.95) * mm, "end": v(34.2, -1.55) * mm});
            skLineSegment(sketch, "E841", {"start": v(34.2, -1.55) * mm, "end": v(34.2, -1.15) * mm});
            skLineSegment(sketch, "E842", {"start": v(34.2, -1.15) * mm, "end": v(34.02, 0.05) * mm});
            skLineSegment(sketch, "E843", {"start": v(34.02, 0.05) * mm, "end": v(33.6, 1.09) * mm});
            skLineSegment(sketch, "E844", {"start": v(33.6, 1.09) * mm, "end": v(33.47, 1.26) * mm});
            skLineSegment(sketch, "E845", {"start": v(33.47, 1.26) * mm, "end": v(33.35, 1.43) * mm});
            skLineSegment(sketch, "E846", {"start": v(33.35, 1.43) * mm, "end": v(32.6, 2.02) * mm});
            skLineSegment(sketch, "E847", {"start": v(32.6, 2.02) * mm, "end": v(31.75, 2.28) * mm});
            skLineSegment(sketch, "E848", {"start": v(31.75, 2.28) * mm, "end": v(31.46, 2.28) * mm});
            skLineSegment(sketch, "E849", {"start": v(31.46, 2.28) * mm, "end": v(31.25, 2.28) * mm});
            skLineSegment(sketch, "E850", {"start": v(31.25, 2.28) * mm, "end": v(30.6, 2.14) * mm});
            skLineSegment(sketch, "E851", {"start": v(30.6, 2.14) * mm, "end": v(29.96, 1.8) * mm});
            skLineSegment(sketch, "E852", {"start": v(29.96, 1.8) * mm, "end": v(29.84, 1.71) * mm});
            skLineSegment(sketch, "E853", {"start": v(29.84, 1.71) * mm, "end": v(29.72, 1.62) * mm});
            skLineSegment(sketch, "E854", {"start": v(29.72, 1.62) * mm, "end": v(29.25, 1.08) * mm});
            skLineSegment(sketch, "E855", {"start": v(29.25, 1.08) * mm, "end": v(28.96, 0.45) * mm});
            skLineSegment(sketch, "E856", {"start": v(28.96, 0.45) * mm, "end": v(28.93, 0.31) * mm});
            skSolve(sketch);
        }
        {
            var Q0;
            Q0=qCreatedBy(makeId("Top.planeOp"),FACE);
            var sketch = newSketch(context, id + "F1", { "sketchPlane" : qUnion([Q0])});
            skLineSegment(sketch, "E857.bottom", {"start": v(42.5, -20) * mm, "end": v(-42.5, -20) * mm});
            skLineSegment(sketch, "E857.top", {"start": v(42.5, 20) * mm, "end": v(-42.5, 20) * mm});
            skLineSegment(sketch, "E857.left", {"start": v(42.5, -20) * mm, "end": v(42.5, 20) * mm});
            skLineSegment(sketch, "E857.right", {"start": v(-42.5, -20) * mm, "end": v(-42.5, 20) * mm});
            skPoint(sketch, "E857.middle", {"position": v(0, 0) * mm});
            skSolve(sketch);
        }
        {
            var Q0;
            Q0 = qSketchRegion(id + "F1", true);
            extrude(context, id + "F2", {"entities" : qUnion([Q0]), "depth" : -5 * mm});
        }
        {
            var Q0;
            Q0 = qSketchRegion(id + "F0", true);
            extrude(context, id + "F3", {"entities" : qUnion([Q0]), "depth" : -3 * mm});
        }
        {
            var Q0;
            Q0=makeQuery(id+"F2.opExtrude","SWEPT_EDGE",EDGE,{"disambiguationData":[OSD([sQuery(id+"F1.wireOp",EDGE,"E857.bottom"),sQuery(id+"F1.wireOp",EDGE,"E857.right")])]});
            var Q1;
            Q1=makeQuery(id+"F2.opExtrude","SWEPT_EDGE",EDGE,{"disambiguationData":[OSD([sQuery(id+"F1.wireOp",EDGE,"E857.top"),sQuery(id+"F1.wireOp",EDGE,"E857.right")])]});
            var Q2;
            Q2=makeQuery(id+"F2.opExtrude","SWEPT_EDGE",EDGE,{"disambiguationData":[OSD([sQuery(id+"F1.wireOp",EDGE,"E857.bottom"),sQuery(id+"F1.wireOp",EDGE,"E857.left")])]});
            var Q3;
            Q3=makeQuery(id+"F2.opExtrude","SWEPT_EDGE",EDGE,{"disambiguationData":[OSD([sQuery(id+"F1.wireOp",EDGE,"E857.top"),sQuery(id+"F1.wireOp",EDGE,"E857.left")])]});
            fillet(context, id + "F4", {"entities" : qUnion([Q0, Q1, Q2, Q3]), "radius" : 3 * mm, "tangentPropagation" : true, "allowEdgeOverflow" : false});
        }
        {
            var Q0;
            Q0=makeQuery(id+"F2.opExtrude","CAP_FACE",FACE,{"disambiguationData":[OSD([sQuery(id+"F1.wireOp",EDGE,"E857.bottom"),sQuery(id+"F1.wireOp",EDGE,"E857.top"),sQuery(id+"F1.wireOp",EDGE,"E857.left"),sQuery(id+"F1.wireOp",EDGE,"E857.right")])],"isStart":true});
            fillet(context, id + "F5", {"entities" : qUnion([Q0]), "radius" : 1 * mm, "tangentPropagation" : true, "allowEdgeOverflow" : false});
        }
    });
